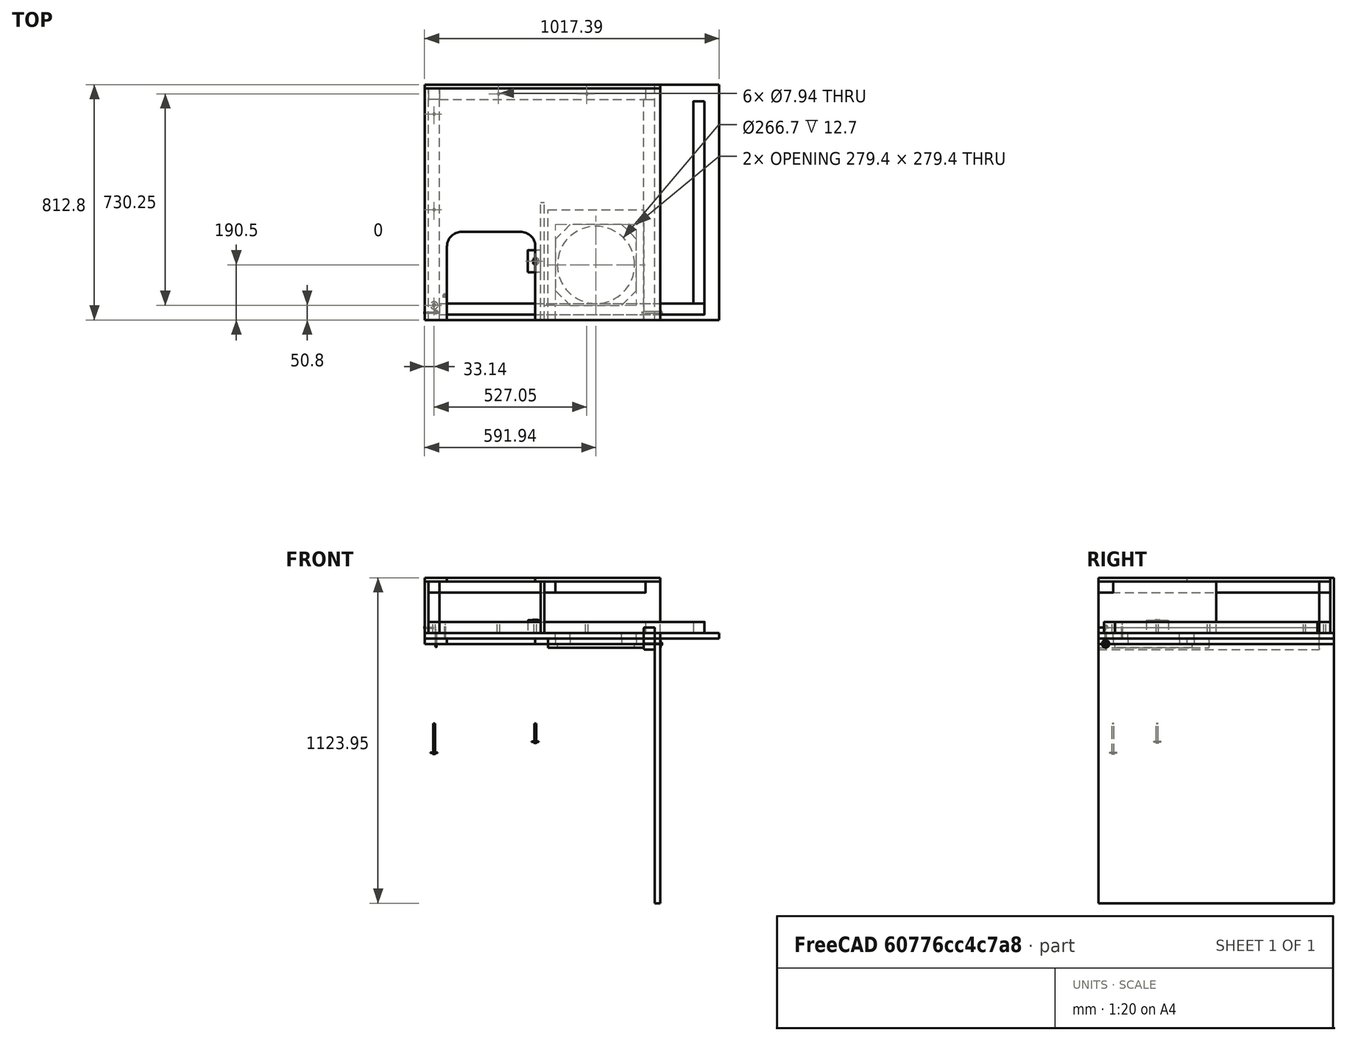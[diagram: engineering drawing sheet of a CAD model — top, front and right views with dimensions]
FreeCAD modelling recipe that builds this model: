
FCSTD DOCUMENT  (FreeCAD 0.20R)
Label: Assembly
License: Creative Commons Attribution
LicenseURL: http://creativecommons.org/licenses/by/4.0/
objects: App::Link×135, Sketcher::SketchObject×20, Part::Extrusion×20, App::LinkGroup×17, Part::Feature×9, Part::Cut×6, App::DocumentObjectGroup×1, Part::Cylinder×1, Mesh::Feature×1
note: 56 computed .brp shape members not serialized (recipe doc carries the construction recipe); baked Part::Feature solids carry a one-line shape summary decoded from their .brp

FEATURE [Sketcher::SketchObject] Sketch004  label="Sketch_H_Inlet_Wall"
  FullyConstrained = false
  sketch-geometry (12):
    g0: LineSegment StartX=0 StartY=0 StartZ=0 EndX=812.8 EndY=0 EndZ=0
    g1: LineSegment StartX=812.8 StartY=0 StartZ=0 EndX=812.8 EndY=812.8 EndZ=0
    g2: LineSegment StartX=812.8 StartY=812.8 StartZ=0 EndX=0 EndY=812.8 EndZ=0
    g3: LineSegment StartX=0 StartY=812.8 StartZ=0 EndX=0 EndY=0 EndZ=0
    g4: LineSegment StartX=730.25 StartY=101.6 StartZ=0 EndX=730.25 EndY=279.4 EndZ=0
    g5: LineSegment StartX=730.25 StartY=279.4 StartZ=0 EndX=679.45 EndY=330.2 EndZ=0
    g6: LineSegment StartX=679.45 StartY=330.2 StartZ=0 EndX=501.65 EndY=330.2 EndZ=0
    g7: LineSegment StartX=501.65 StartY=330.2 StartZ=0 EndX=450.85 EndY=279.4 EndZ=0
    g8: LineSegment StartX=450.85 StartY=279.4 StartZ=0 EndX=450.85 EndY=101.6 EndZ=0
    g9: LineSegment StartX=450.85 StartY=101.6 StartZ=0 EndX=501.65 EndY=50.8 EndZ=0
    g10: LineSegment StartX=501.65 StartY=50.8 StartZ=0 EndX=679.45 EndY=50.8 EndZ=0
    g11: LineSegment StartX=679.45 StartY=50.8 StartZ=0 EndX=730.25 EndY=101.6 EndZ=0
  constraints (35):
    c: Coincident(g0,g1)
    c: Coincident(g1,g2)
    c: Coincident(g2,g3)
    c: Coincident(g3,g0)
    c: Horizontal(g0)
    c: Horizontal(g2)
    c: Vertical(g1)
    c: Vertical(g3)
    c: Coincident(g0,g-1)
    c: DistanceX(g0,g0) = 812.8
    c: DistanceY(g3,g3) = 812.8
    c: Vertical(g4)
    c: Coincident(g4,g5)
    c: Coincident(g5,g6)
    c: Horizontal(g6)
    c: Coincident(g6,g7)
    c: Coincident(g7,g8)
    c: Vertical(g8)
    c: Coincident(g8,g9)
    c: Coincident(g9,g10)
    c: Horizontal(g10)
    c: Coincident(g10,g11)
    c: Coincident(g11,g4)
    c: DistanceX(g4,g0) = 82.55
    c: DistanceY(g0,g10) = 50.8
    c: DistanceX(g8,g9) = 50.8
    c: Perpendicular(g7,g9)
    c: DistanceX(g8,g4) = 279.4
    c: Equal(g8,g6)
    c: Equal(g6,g4)
    c: Equal(g4,g10)
    c: Equal(g9,g7)
    c: Equal(g7,g5)
    c: Equal(g5,g11)
    c: DistanceY(g9,g8) = 50.8
FEATURE [Part::Extrusion] Extrude004  label="Part_H_Inlet_Wall"
  Base = -> Sketch004
  Dir = (0,0,1)
  DirMode = 2
  FaceMakerClass = Part::FaceMakerBullseye
  LengthFwd = 19.05
  LengthRev = 0
  Solid = true
  Symmetric = false
FEATURE [Sketcher::SketchObject] Sketch005  label="Sketch_I_Fan_Mount"
  FullyConstrained = false
  sketch-geometry (5):
    g0: LineSegment StartX=0 StartY=0 StartZ=0 EndX=330.2 EndY=0 EndZ=0
    g1: LineSegment StartX=330.2 StartY=0 StartZ=0 EndX=330.2 EndY=381 EndZ=0
    g2: LineSegment StartX=330.2 StartY=381 StartZ=0 EndX=0 EndY=381 EndZ=0
    g3: LineSegment StartX=0 StartY=381 StartZ=0 EndX=0 EndY=0 EndZ=0
    g4: Circle CenterX=165.1 CenterY=190.5 CenterZ=0 NormalX=0 NormalY=0 NormalZ=1 AngleXU=0 Radius=133.35
  constraints (13):
    c: Coincident(g0,g1)
    c: Coincident(g1,g2)
    c: Coincident(g2,g3)
    c: Coincident(g3,g0)
    c: Horizontal(g0)
    c: Horizontal(g2)
    c: Vertical(g1)
    c: Vertical(g3)
    c: Coincident(g0,g-1)
    c: DistanceY(g3,g3) = 381
    c: DistanceX(g0,g0) = 330.2
    c: Diameter(g4) = 266.7
    c: Symmetric(g0,g1,g4)
FEATURE [Part::Extrusion] Extrude005  label="Part_I_Fan_Mount"
  Base = -> Sketch005
  Dir = (0,0,1)
  DirMode = 2
  FaceMakerClass = Part::FaceMakerBullseye
  LengthFwd = 12.7
  LengthRev = 0
  Placement = pos=(755.65,0,-19.05) rot=(0,1,0;3.14159rad)
  Solid = true
  Symmetric = false
FEATURE [Part::Feature] Part__Feature  label="FAN_W2E250-HJ32-01"
  Placement = pos=(590.55,190.5,-19.05) rot=(1,0,0;1.5708rad)
  shape: bbox 300.2 x 295.3 x 80.4 mm, 902 faces, 0 solids (baked)
FEATURE [Sketcher::SketchObject] Sketch006  label="Sketch_2x2_rail"
  FullyConstrained = false
  sketch-geometry (8):
    g0: LineSegment StartX=0 StartY=34.925 StartZ=0 EndX=0 EndY=3.175 EndZ=0
    g1: ArcOfCircle CenterX=3.175 CenterY=34.925 CenterZ=0 NormalX=0 NormalY=0 NormalZ=1 AngleXU=0 Radius=3.175 StartAngle=1.5708 EndAngle=3.14159
    g2: LineSegment StartX=3.175 StartY=38.1 StartZ=0 EndX=34.925 EndY=38.1 EndZ=0
    g3: ArcOfCircle CenterX=34.925 CenterY=34.925 CenterZ=0 NormalX=0 NormalY=0 NormalZ=1 AngleXU=0 Radius=3.175 StartAngle=4e-16 EndAngle=1.5708
    g4: LineSegment StartX=38.1 StartY=34.925 StartZ=0 EndX=38.1 EndY=3.175 EndZ=0
    g5: ArcOfCircle CenterX=34.925 CenterY=3.175 CenterZ=0 NormalX=0 NormalY=0 NormalZ=1 AngleXU=0 Radius=3.175 StartAngle=4.71239 EndAngle=6.28319
    g6: LineSegment StartX=34.925 StartY=0 StartZ=0 EndX=3.175 EndY=0 EndZ=0
    g7: ArcOfCircle CenterX=3.175 CenterY=3.175 CenterZ=0 NormalX=0 NormalY=0 NormalZ=1 AngleXU=0 Radius=3.175 StartAngle=3.14159 EndAngle=4.71239
  constraints (22):
    c: Vertical(g0)
    c: Tangent(g0,g1) = -1.5708
    c: Radius(g1) = 3.175
    c: Angle(g1) = 1.5708
    c: Coincident(g2,g1)
    c: Horizontal(g2)
    c: Tangent(g2,g3) = 1.5708
    c: Coincident(g4,g3)
    c: Vertical(g4)
    c: Tangent(g5,g4) = 1.5708
    c: Horizontal(g6)
    c: Tangent(g6,g5) = 1.5708
    c: Tangent(g7,g6) = 1.5708
    c: Tangent(g7,g0) = -1.5708
    c: Equal(g1,g7)
    c: Equal(g7,g3)
    c: Equal(g2,g0)
    c: Equal(g0,g6)
    c: Equal(g6,g4)
    c: PointOnObject(g-1,g0)
    c: PointOnObject(g6,g-1)
    c: DistanceX(g0,g4) = 38.1
FEATURE [Part::Extrusion] Extrude006  label="IF_A"
  Base = -> Sketch006
  Dir = (0,0,1)
  DirMode = 2
  FaceMakerClass = Part::FaceMakerBullseye
  LengthFwd = 762
  LengthRev = 0
  Placement = pos=(793.75,0,1e-14) rot=(0.57735,-0.57735,-0.57735;4.18879rad)
  Solid = true
  Symmetric = false
FEATURE [Sketcher::SketchObject] Sketch007  label="Sketch_H_Inlet_Wall001"
  FullyConstrained = false
  sketch-geometry (12):
    g0: LineSegment StartX=0 StartY=0 StartZ=0 EndX=330.2 EndY=0 EndZ=0
    g1: LineSegment StartX=330.2 StartY=0 StartZ=0 EndX=330.2 EndY=381 EndZ=0
    g2: LineSegment StartX=330.2 StartY=381 StartZ=0 EndX=0 EndY=381 EndZ=0
    g3: LineSegment StartX=0 StartY=381 StartZ=0 EndX=0 EndY=0 EndZ=0
    g4: LineSegment StartX=304.8 StartY=101.6 StartZ=0 EndX=304.8 EndY=279.4 EndZ=0
    g5: LineSegment StartX=304.8 StartY=279.4 StartZ=0 EndX=254 EndY=330.2 EndZ=0
    g6: LineSegment StartX=254 StartY=330.2 StartZ=0 EndX=76.2 EndY=330.2 EndZ=0
    g7: LineSegment StartX=76.2 StartY=330.2 StartZ=0 EndX=25.4 EndY=279.4 EndZ=0
    g8: LineSegment StartX=25.4 StartY=279.4 StartZ=0 EndX=25.4 EndY=101.6 EndZ=0
    g9: LineSegment StartX=25.4 StartY=101.6 StartZ=0 EndX=76.2 EndY=50.8 EndZ=0
    g10: LineSegment StartX=76.2 StartY=50.8 StartZ=0 EndX=254 EndY=50.8 EndZ=0
    g11: LineSegment StartX=254 StartY=50.8 StartZ=0 EndX=304.8 EndY=101.6 EndZ=0
  constraints (35):
    c: Coincident(g0,g1)
    c: Coincident(g1,g2)
    c: Coincident(g2,g3)
    c: Coincident(g3,g0)
    c: Horizontal(g0)
    c: Horizontal(g2)
    c: Vertical(g1)
    c: Vertical(g3)
    c: Coincident(g0,g-1)
    c: DistanceX(g0,g0) = 330.2
    c: DistanceY(g3,g3) = 381
    c: Vertical(g4)
    c: Coincident(g4,g5)
    c: Coincident(g5,g6)
    c: Horizontal(g6)
    c: Coincident(g6,g7)
    c: Coincident(g7,g8)
    c: Vertical(g8)
    c: Coincident(g8,g9)
    c: Coincident(g9,g10)
    c: Horizontal(g10)
    c: Coincident(g10,g11)
    c: Coincident(g11,g4)
    c: DistanceX(g7,g4) = 279.4
    c: DistanceX(g4,g0) = 25.4
    c: DistanceY(g0,g10) = 50.8
    c: DistanceX(g8,g9) = 50.8
    c: Perpendicular(g11,g9)
    c: Equal(g6,g10)
    c: Equal(g10,g8)
    c: Equal(g8,g4)
    c: Equal(g7,g11)
    c: Equal(g11,g9)
    c: Equal(g9,g5)
    c: DistanceY(g9,g8) = 50.8
FEATURE [Part::Extrusion] Extrude007  label="Fan_Spacer"
  Base = -> Sketch007
  Dir = (0,0,1)
  DirMode = 2
  FaceMakerClass = Part::FaceMakerBullseye
  LengthFwd = 19.05
  LengthRev = 0
  Placement = pos=(755.65,0,4.3e-14) rot=(0,1,0;3.14159rad)
  Solid = true
  Symmetric = false
FEATURE [Part::Feature] Screw_w_Washer_B
  Placement = pos=(38.1,25.4,19.05) rot=(0,1,0;3.14159rad)
  shape: bbox 15.88 x 15.88 x 50.8 mm, 35 faces (baked)
FEATURE [App::Link] Link001  label="Screw_w_Washer_B001"
  LinkPlacement = pos=(38.1,736.601,19.05) rot=(0,1,0;3.14159rad)
  LinkedObject = -> Screw_w_Washer_B
  Placement = pos=(38.1,736.601,19.05) rot=(0,1,0;3.14159rad)
FEATURE [App::Link] Link002  label="Screw_w_Washer_B002"
  LinkPlacement = pos=(38.1,152.4,19.05) rot=(1,0,0;3.14159rad)
  LinkedObject = -> Screw_w_Washer_B
  Placement = pos=(38.1,152.4,19.05) rot=(1,0,0;3.14159rad)
FEATURE [App::Link] Link003  label="Screw_w_Washer_B003"
  LinkPlacement = pos=(38.1,609.6,19.0501) rot=(1,0,0;3.14159rad)
  LinkedObject = -> Screw_w_Washer_B
  Placement = pos=(38.1,609.6,19.0501) rot=(1,0,0;3.14159rad)
FEATURE [App::Link] Link004  label="Screw_w_Washer_B004"
  LinkPlacement = pos=(38.1,304.8,19.05) rot=(0,1,0;3.14159rad)
  LinkedObject = -> Screw_w_Washer_B
  Placement = pos=(38.1,304.8,19.05) rot=(0,1,0;3.14159rad)
FEATURE [App::Link] Link005  label="Screw_w_Washer_B005"
  LinkPlacement = pos=(38.1,457.2,19.05) rot=(0,1,0;3.14159rad)
  LinkedObject = -> Screw_w_Washer_B
  Placement = pos=(38.1,457.2,19.05) rot=(0,1,0;3.14159rad)
FEATURE [App::Link] Link006  label="Screw_w_Washer_B006"
  LinkTransform = true
  LinkedObject = -> Screw_w_Washer_B
FEATURE [App::Link] Link007  label="Screw_w_Washer_B007"
  LinkTransform = true
  LinkedObject = -> Link001
FEATURE [App::Link] Link008  label="Screw_w_Washer_B008"
  LinkTransform = true
  LinkedObject = -> Link002
FEATURE [App::Link] Link009  label="Screw_w_Washer_B009"
  LinkTransform = true
  LinkedObject = -> Link003
FEATURE [App::Link] Link010  label="Screw_w_Washer_B010"
  LinkTransform = true
  LinkedObject = -> Link004
FEATURE [App::Link] Link011  label="Screw_w_Washer_B011"
  LinkTransform = true
  LinkedObject = -> Link005
FEATURE [App::LinkGroup] LinkGroup
  ElementList = -> [Link006,Link007,Link008,Link009,Link010,Link011]
  LinkMode = 1
  Placement = pos=(736.6,-6.10352e-05,0) rot=(0,0,1;0rad)
FEATURE [App::Link] Link012  label="Screw_w_Washer_B012"
  LinkPlacement = pos=(450.85,50.8,-31.75) rot=(0,0,1;0rad)
  LinkedObject = -> Screw_w_Washer_B
  Placement = pos=(450.85,50.8,-31.75) rot=(0,0,1;0rad)
FEATURE [App::Link] Link013  label="Screw_w_Washer_B013"
  LinkPlacement = pos=(590.55,355.6,-31.75) rot=(0,0,1;1.5708rad)
  LinkedObject = -> Screw_w_Washer_B
  Placement = pos=(590.55,355.6,-31.75) rot=(0,0,1;1.5708rad)
FEATURE [App::Link] Link014  label="Screw_w_Washer_B014"
  LinkPlacement = pos=(438.15,190.5,-31.75) rot=(0,0,1;3.14159rad)
  LinkedObject = -> Screw_w_Washer_B
  Placement = pos=(438.15,190.5,-31.75) rot=(0,0,1;3.14159rad)
FEATURE [App::Link] Link015  label="Screw_w_Washer_B015"
  LinkPlacement = pos=(450.85,330.2,-31.75) rot=(0,0,-1;1.5708rad)
  LinkedObject = -> Screw_w_Washer_B
  Placement = pos=(450.85,330.2,-31.75) rot=(0,0,-1;1.5708rad)
FEATURE [App::Link] Link016  label="Screw_w_Washer_B016"
  LinkPlacement = pos=(590.55,25.3999,-31.75) rot=(0,0,1;0rad)
  LinkedObject = -> Screw_w_Washer_B
  Placement = pos=(590.55,25.3999,-31.75) rot=(0,0,1;0rad)
FEATURE [App::Link] Link017  label="Screw_w_Washer_B017"
  LinkPlacement = pos=(730.25,50.7999,-31.75) rot=(0,0,1;1.5708rad)
  LinkedObject = -> Screw_w_Washer_B
  Placement = pos=(730.25,50.7999,-31.75) rot=(0,0,1;1.5708rad)
FEATURE [App::Link] Link018  label="Screw_w_Washer_B018"
  LinkPlacement = pos=(742.95,190.5,-31.75) rot=(0,0,1;3.14159rad)
  LinkedObject = -> Screw_w_Washer_B
  Placement = pos=(742.95,190.5,-31.75) rot=(0,0,1;3.14159rad)
FEATURE [App::Link] Link019  label="Screw_w_Washer_B019"
  LinkPlacement = pos=(730.25,330.2,-31.75) rot=(0,0,1;3.14159rad)
  LinkedObject = -> Screw_w_Washer_B
  Placement = pos=(730.25,330.2,-31.75) rot=(0,0,1;3.14159rad)
FEATURE [App::DocumentObjectGroup] Group
  Group = -> [Link012,Link013,Link014,Link015,Link016,Link017,Link018,Link019,Part__Feature,Extrude005,Extrude007]
FEATURE [App::LinkGroup] LinkGroup001
  ElementList = -> [Group]
  LinkMode = 0
  Placement = pos=(3.05176e-05,-0.000106812,6.67572e-05) rot=(0,0,1;0rad)
FEATURE [Sketcher::SketchObject] Sketch  label="Sketch_2x2_rail001"
  FullyConstrained = false
  sketch-geometry (8):
    g0: LineSegment StartX=0 StartY=34.925 StartZ=0 EndX=0 EndY=3.175 EndZ=0
    g1: ArcOfCircle CenterX=3.175 CenterY=34.925 CenterZ=0 NormalX=0 NormalY=0 NormalZ=1 AngleXU=0 Radius=3.175 StartAngle=1.5708 EndAngle=3.14159
    g2: LineSegment StartX=3.175 StartY=38.1 StartZ=0 EndX=34.925 EndY=38.1 EndZ=0
    g3: ArcOfCircle CenterX=34.925 CenterY=34.925 CenterZ=0 NormalX=0 NormalY=0 NormalZ=1 AngleXU=0 Radius=3.175 StartAngle=2.2e-15 EndAngle=1.5708
    g4: LineSegment StartX=38.1 StartY=34.925 StartZ=0 EndX=38.1 EndY=3.175 EndZ=0
    g5: ArcOfCircle CenterX=34.925 CenterY=3.175 CenterZ=0 NormalX=0 NormalY=0 NormalZ=1 AngleXU=0 Radius=3.175 StartAngle=4.71239 EndAngle=6.28319
    g6: LineSegment StartX=34.925 StartY=0 StartZ=0 EndX=3.175 EndY=0 EndZ=0
    g7: ArcOfCircle CenterX=3.175 CenterY=3.175 CenterZ=0 NormalX=0 NormalY=0 NormalZ=1 AngleXU=0 Radius=3.175 StartAngle=3.14159 EndAngle=4.71239
  constraints (22):
    c: Vertical(g0)
    c: Tangent(g0,g1) = -1.5708
    c: Radius(g1) = 3.175
    c: Angle(g1) = 1.5708
    c: Coincident(g2,g1)
    c: Horizontal(g2)
    c: Tangent(g2,g3) = 1.5708
    c: Coincident(g4,g3)
    c: Vertical(g4)
    c: Tangent(g5,g4) = 1.5708
    c: Horizontal(g6)
    c: Tangent(g6,g5) = 1.5708
    c: Tangent(g7,g6) = 1.5708
    c: Tangent(g7,g0) = -1.5708
    c: Equal(g1,g7)
    c: Equal(g7,g3)
    c: Equal(g2,g0)
    c: Equal(g0,g6)
    c: Equal(g6,g4)
    c: PointOnObject(g-1,g0)
    c: PointOnObject(g6,g-1)
    c: DistanceX(g0,g4) = 38.1
FEATURE [Part::Extrusion] Extrude  label="BF_A"
  Base = -> Sketch
  Dir = (0,0,1)
  DirMode = 2
  FaceMakerClass = Part::FaceMakerBullseye
  LengthFwd = 800.1
  LengthRev = 0
  Placement = pos=(12.7,4.4e-14,196.85) rot=(-1,0,0;1.5708rad)
  Solid = true
  Symmetric = false
FEATURE [Sketcher::SketchObject] Sketch008  label="Sketch_D_Baffle_Ext_Wall"
  FullyConstrained = false
  sketch-geometry (10):
    g0: LineSegment StartX=0 StartY=0 StartZ=0 EndX=0 EndY=800.1 EndZ=0
    g1: LineSegment StartX=0 StartY=800.1 StartZ=0 EndX=812.8 EndY=800.1 EndZ=0
    g2: LineSegment StartX=812.8 StartY=800.1 StartZ=0 EndX=812.8 EndY=0 EndZ=0
    g3: LineSegment StartX=812.8 StartY=0 StartZ=0 EndX=736.6 EndY=0 EndZ=0
    g4: LineSegment StartX=736.6 StartY=0 StartZ=0 EndX=736.6 EndY=254 EndZ=0
    g5: LineSegment StartX=685.8 StartY=304.8 StartZ=0 EndX=482.6 EndY=304.8 EndZ=0
    g6: LineSegment StartX=431.8 StartY=254 StartZ=0 EndX=431.8 EndY=0 EndZ=0
    g7: LineSegment StartX=431.8 StartY=0 StartZ=0 EndX=0 EndY=0 EndZ=0
    g8: ArcOfCircle CenterX=482.6 CenterY=254 CenterZ=0 NormalX=0 NormalY=0 NormalZ=1 AngleXU=0 Radius=50.8 StartAngle=1.5708 EndAngle=3.14159
    g9: ArcOfCircle CenterX=685.8 CenterY=254 CenterZ=0 NormalX=0 NormalY=0 NormalZ=1 AngleXU=0 Radius=50.8 StartAngle=0 EndAngle=1.5708
  constraints (27):
    c: Coincident(g-1,g0)
    c: PointOnObject(g0,g-2)
    c: Coincident(g0,g1)
    c: Horizontal(g1)
    c: Coincident(g1,g2)
    c: PointOnObject(g2,g-1)
    c: Vertical(g2)
    c: Coincident(g2,g3)
    c: PointOnObject(g3,g-1)
    c: Coincident(g3,g4)
    c: Vertical(g4)
    c: Horizontal(g5)
    c: PointOnObject(g6,g-1)
    c: Vertical(g6)
    c: Coincident(g6,g7)
    c: Coincident(g7,g0)
    c: DistanceY(g0,g0) = 800.1
    c: DistanceX(g1,g1) = 812.8
    c: DistanceX(g3,g3) = 76.2
    c: DistanceX(g6,g3) = 304.8
    c: DistanceY(g6,g5) = 304.8
    c: Equal(g8,g9)
    c: Tangent(g8,g6) = -1.5708
    c: Tangent(g9,g4) = -1.5708
    c: Tangent(g9,g5) = -1.5708
    c: Tangent(g8,g5) = -1.5708
    c: Radius(g8) = 50.8
FEATURE [Part::Extrusion] Extrude008  label="Part_D_Baffle_Ext_Wall_001"
  Base = -> Sketch008
  Dir = (0,0,1)
  DirMode = 2
  FaceMakerClass = Part::FaceMakerBullseye
  LengthFwd = 12.7
  LengthRev = 0
  Placement = pos=(812.8,0,209.55) rot=(0,1,0;3.14159rad)
  Solid = true
  Symmetric = false
FEATURE [Sketcher::SketchObject] Sketch009  label="Sketch_G_Baffle_Half_Wall"
  FullyConstrained = false
  sketch-geometry (4):
    g0: LineSegment StartX=0 StartY=0 StartZ=0 EndX=406.4 EndY=0 EndZ=0
    g1: LineSegment StartX=406.4 StartY=0 StartZ=0 EndX=406.4 EndY=177.8 EndZ=0
    g2: LineSegment StartX=406.4 StartY=177.8 StartZ=0 EndX=0 EndY=177.8 EndZ=0
    g3: LineSegment StartX=0 StartY=177.8 StartZ=0 EndX=0 EndY=0 EndZ=0
  constraints (11):
    c: Coincident(g0,g1)
    c: Coincident(g1,g2)
    c: Coincident(g2,g3)
    c: Coincident(g3,g0)
    c: Horizontal(g0)
    c: Horizontal(g2)
    c: Vertical(g1)
    c: Vertical(g3)
    c: Coincident(g0,g-1)
    c: DistanceY(g3,g3) = 177.8
    c: DistanceX(g0,g0) = 406.4
FEATURE [Part::Extrusion] Extrude009  label="Part_G_Baffle_Half_Wall_001"
  Base = -> Sketch009
  Dir = (0,0,1)
  DirMode = 2
  FaceMakerClass = Part::FaceMakerBullseye
  LengthFwd = 12.7
  LengthRev = 0
  Placement = pos=(400.05,-8.5e-14,19.05) rot=(0.57735,0.57735,0.57735;2.0944rad)
  Solid = true
  Symmetric = false
FEATURE [Sketcher::SketchObject] Sketch010  label="Sketch_E_Baffle_Top"
  FullyConstrained = false
  sketch-geometry (4):
    g0: LineSegment StartX=0 StartY=0 StartZ=0 EndX=812.8 EndY=0 EndZ=0
    g1: LineSegment StartX=812.8 StartY=0 StartZ=0 EndX=812.8 EndY=190.5 EndZ=0
    g2: LineSegment StartX=812.8 StartY=190.5 StartZ=0 EndX=0 EndY=190.5 EndZ=0
    g3: LineSegment StartX=0 StartY=190.5 StartZ=0 EndX=0 EndY=0 EndZ=0
  constraints (11):
    c: Coincident(g0,g1)
    c: Coincident(g1,g2)
    c: Coincident(g2,g3)
    c: Coincident(g3,g0)
    c: Horizontal(g0)
    c: Horizontal(g2)
    c: Vertical(g1)
    c: Vertical(g3)
    c: Coincident(g0,g-1)
    c: DistanceY(g3,g3) = 190.5
    c: DistanceX(g0,g0) = 812.8
FEATURE [Part::Extrusion] Extrude010  label="Part_E_Baffle_Top_001"
  Base = -> Sketch010
  Dir = (0,0,1)
  DirMode = 2
  FaceMakerClass = Part::FaceMakerBullseye
  LengthFwd = 12.7
  LengthRev = 0
  Placement = pos=(0,812.8,19.05) rot=(1,0,0;1.5708rad)
  Solid = true
  Symmetric = false
FEATURE [Sketcher::SketchObject] Sketch012  label="Sketch_F_Baffle_Side_Wall"
  FullyConstrained = false
  sketch-geometry (4):
    g0: LineSegment StartX=0 StartY=0 StartZ=0 EndX=800.1 EndY=0 EndZ=0
    g1: LineSegment StartX=800.1 StartY=0 StartZ=0 EndX=800.1 EndY=177.8 EndZ=0
    g2: LineSegment StartX=800.1 StartY=177.8 StartZ=0 EndX=0 EndY=177.8 EndZ=0
    g3: LineSegment StartX=0 StartY=177.8 StartZ=0 EndX=0 EndY=0 EndZ=0
  constraints (11):
    c: Coincident(g0,g1)
    c: Coincident(g1,g2)
    c: Coincident(g2,g3)
    c: Coincident(g3,g0)
    c: Horizontal(g0)
    c: Horizontal(g2)
    c: Vertical(g1)
    c: Vertical(g3)
    c: Coincident(g0,g-1)
    c: DistanceY(g3,g3) = 177.8
    c: DistanceX(g0,g0) = 800.1
FEATURE [Part::Extrusion] Extrude012  label="Part_F_Baffle_Side_Wall_001"
  Base = -> Sketch012
  Dir = (0,0,1)
  DirMode = 2
  FaceMakerClass = Part::FaceMakerBullseye
  LengthFwd = 12.7
  LengthRev = 0
  Placement = pos=(-4e-15,-8e-15,19.05) rot=(0.57735,0.57735,0.57735;2.0944rad)
  Solid = true
  Symmetric = false
FEATURE [Sketcher::SketchObject] Sketch013  label="Sketch_2x2_rail002"
  FullyConstrained = false
  sketch-geometry (8):
    g0: LineSegment StartX=0 StartY=34.925 StartZ=0 EndX=0 EndY=3.175 EndZ=0
    g1: ArcOfCircle CenterX=3.175 CenterY=34.925 CenterZ=0 NormalX=0 NormalY=0 NormalZ=1 AngleXU=0 Radius=3.175 StartAngle=1.5708 EndAngle=3.14159
    g2: LineSegment StartX=3.175 StartY=38.1 StartZ=0 EndX=34.925 EndY=38.1 EndZ=0
    g3: ArcOfCircle CenterX=34.925 CenterY=34.925 CenterZ=0 NormalX=0 NormalY=0 NormalZ=1 AngleXU=0 Radius=3.175 StartAngle=1.1e-15 EndAngle=1.5708
    g4: LineSegment StartX=38.1 StartY=34.925 StartZ=0 EndX=38.1 EndY=3.175 EndZ=0
    g5: ArcOfCircle CenterX=34.925 CenterY=3.175 CenterZ=0 NormalX=0 NormalY=0 NormalZ=1 AngleXU=0 Radius=3.175 StartAngle=4.71239 EndAngle=6.28319
    g6: LineSegment StartX=34.925 StartY=4e-16 StartZ=0 EndX=3.175 EndY=4e-16 EndZ=0
    g7: ArcOfCircle CenterX=3.175 CenterY=3.175 CenterZ=0 NormalX=0 NormalY=0 NormalZ=1 AngleXU=0 Radius=3.175 StartAngle=3.14159 EndAngle=4.71239
  constraints (22):
    c: Vertical(g0)
    c: Tangent(g0,g1) = -1.5708
    c: Radius(g1) = 3.175
    c: Angle(g1) = 1.5708
    c: Coincident(g2,g1)
    c: Horizontal(g2)
    c: Tangent(g2,g3) = 1.5708
    c: Coincident(g4,g3)
    c: Vertical(g4)
    c: Tangent(g5,g4) = 1.5708
    c: Horizontal(g6)
    c: Tangent(g6,g5) = 1.5708
    c: Tangent(g7,g6) = 1.5708
    c: Tangent(g7,g0) = -1.5708
    c: Equal(g1,g7)
    c: Equal(g7,g3)
    c: Equal(g2,g0)
    c: Equal(g0,g6)
    c: Equal(g6,g4)
    c: PointOnObject(g-1,g0)
    c: PointOnObject(g6,g-1)
    c: DistanceX(g0,g4) = 38.1
FEATURE [Part::Extrusion] Extrude013  label="BF_C"
  Base = -> Sketch013
  Dir = (0,0,1)
  DirMode = 2
  FaceMakerClass = Part::FaceMakerBullseye
  LengthFwd = 139.7
  LengthRev = 0
  Placement = pos=(12.7,762,19.05) rot=(0,0,1;0rad)
  Solid = true
  Symmetric = false
FEATURE [Sketcher::SketchObject] Sketch014  label="Sketch_2x2_rail003"
  FullyConstrained = false
  sketch-geometry (8):
    g0: LineSegment StartX=0 StartY=34.925 StartZ=0 EndX=0 EndY=3.175 EndZ=0
    g1: ArcOfCircle CenterX=3.175 CenterY=34.925 CenterZ=0 NormalX=0 NormalY=0 NormalZ=1 AngleXU=0 Radius=3.175 StartAngle=1.5708 EndAngle=3.14159
    g2: LineSegment StartX=3.175 StartY=38.1 StartZ=0 EndX=34.925 EndY=38.1 EndZ=0
    g3: ArcOfCircle CenterX=34.925 CenterY=34.925 CenterZ=0 NormalX=0 NormalY=0 NormalZ=1 AngleXU=0 Radius=3.175 StartAngle=9e-16 EndAngle=1.5708
    g4: LineSegment StartX=38.1 StartY=34.925 StartZ=0 EndX=38.1 EndY=3.175 EndZ=0
    g5: ArcOfCircle CenterX=34.925 CenterY=3.175 CenterZ=0 NormalX=0 NormalY=0 NormalZ=1 AngleXU=0 Radius=3.175 StartAngle=4.71239 EndAngle=6.28319
    g6: LineSegment StartX=34.925 StartY=4e-16 StartZ=0 EndX=3.175 EndY=4e-16 EndZ=0
    g7: ArcOfCircle CenterX=3.175 CenterY=3.175 CenterZ=0 NormalX=0 NormalY=0 NormalZ=1 AngleXU=0 Radius=3.175 StartAngle=3.14159 EndAngle=4.71239
  constraints (22):
    c: Vertical(g0)
    c: Tangent(g0,g1) = -1.5708
    c: Radius(g1) = 3.175
    c: Angle(g1) = 1.5708
    c: Coincident(g2,g1)
    c: Horizontal(g2)
    c: Tangent(g2,g3) = 1.5708
    c: Coincident(g4,g3)
    c: Vertical(g4)
    c: Tangent(g5,g4) = 1.5708
    c: Horizontal(g6)
    c: Tangent(g6,g5) = 1.5708
    c: Tangent(g7,g6) = 1.5708
    c: Tangent(g7,g0) = -1.5708
    c: Equal(g1,g7)
    c: Equal(g7,g3)
    c: Equal(g2,g0)
    c: Equal(g0,g6)
    c: Equal(g6,g4)
    c: PointOnObject(g-1,g0)
    c: PointOnObject(g6,g-1)
    c: DistanceX(g0,g4) = 38.1
FEATURE [Part::Extrusion] Extrude014  label="BF_B"
  Base = -> Sketch014
  Dir = (0,0,1)
  DirMode = 2
  FaceMakerClass = Part::FaceMakerBullseye
  LengthFwd = 711.2
  LengthRev = 0
  Placement = pos=(50.8,800.1,196.85) rot=(0.57735,-0.57735,0.57735;4.18879rad)
  Solid = true
  Symmetric = false
FEATURE [Sketcher::SketchObject] Sketch015  label="Sketch_2x2_rail004"
  FullyConstrained = false
  sketch-geometry (8):
    g0: LineSegment StartX=0 StartY=34.925 StartZ=0 EndX=0 EndY=3.175 EndZ=0
    g1: ArcOfCircle CenterX=3.175 CenterY=34.925 CenterZ=0 NormalX=0 NormalY=0 NormalZ=1 AngleXU=0 Radius=3.175 StartAngle=1.5708 EndAngle=3.14159
    g2: LineSegment StartX=3.175 StartY=38.1 StartZ=0 EndX=34.925 EndY=38.1 EndZ=0
    g3: ArcOfCircle CenterX=34.925 CenterY=34.925 CenterZ=0 NormalX=0 NormalY=0 NormalZ=1 AngleXU=0 Radius=3.175 StartAngle=1.2e-15 EndAngle=1.5708
    g4: LineSegment StartX=38.1 StartY=34.925 StartZ=0 EndX=38.1 EndY=3.175 EndZ=0
    g5: ArcOfCircle CenterX=34.925 CenterY=3.175 CenterZ=0 NormalX=0 NormalY=0 NormalZ=1 AngleXU=0 Radius=3.175 StartAngle=4.71239 EndAngle=6.28319
    g6: LineSegment StartX=34.925 StartY=0 StartZ=0 EndX=3.175 EndY=0 EndZ=0
    g7: ArcOfCircle CenterX=3.175 CenterY=3.175 CenterZ=0 NormalX=0 NormalY=0 NormalZ=1 AngleXU=0 Radius=3.175 StartAngle=3.14159 EndAngle=4.71239
  constraints (22):
    c: Vertical(g0)
    c: Tangent(g0,g1) = -1.5708
    c: Radius(g1) = 3.175
    c: Angle(g1) = 1.5708
    c: Coincident(g2,g1)
    c: Horizontal(g2)
    c: Tangent(g2,g3) = 1.5708
    c: Coincident(g4,g3)
    c: Vertical(g4)
    c: Tangent(g5,g4) = 1.5708
    c: Horizontal(g6)
    c: Tangent(g6,g5) = 1.5708
    c: Tangent(g7,g6) = 1.5708
    c: Tangent(g7,g0) = -1.5708
    c: Equal(g1,g7)
    c: Equal(g7,g3)
    c: Equal(g2,g0)
    c: Equal(g0,g6)
    c: Equal(g6,g4)
    c: PointOnObject(g-1,g0)
    c: PointOnObject(g6,g-1)
    c: DistanceX(g0,g4) = 38.1
FEATURE [Part::Extrusion] Extrude015  label="BF_D"
  Base = -> Sketch015
  Dir = (0,0,1)
  DirMode = 2
  FaceMakerClass = Part::FaceMakerBullseye
  LengthFwd = 762
  LengthRev = 0
  Placement = pos=(12.7,2.4e-14,19.05) rot=(0.57735,0.57735,0.57735;4.18879rad)
  Solid = true
  Symmetric = false
FEATURE [Sketcher::SketchObject] Sketch016  label="Sketch_2x2_rail005"
  FullyConstrained = false
  sketch-geometry (8):
    g0: LineSegment StartX=0 StartY=34.925 StartZ=0 EndX=0 EndY=3.175 EndZ=0
    g1: ArcOfCircle CenterX=3.175 CenterY=34.925 CenterZ=0 NormalX=0 NormalY=0 NormalZ=1 AngleXU=0 Radius=3.175 StartAngle=1.5708 EndAngle=3.14159
    g2: LineSegment StartX=3.175 StartY=38.1 StartZ=0 EndX=34.925 EndY=38.1 EndZ=0
    g3: ArcOfCircle CenterX=34.925 CenterY=34.925 CenterZ=0 NormalX=0 NormalY=0 NormalZ=1 AngleXU=0 Radius=3.175 StartAngle=2.5e-15 EndAngle=1.5708
    g4: LineSegment StartX=38.1 StartY=34.925 StartZ=0 EndX=38.1 EndY=3.175 EndZ=0
    g5: ArcOfCircle CenterX=34.925 CenterY=3.175 CenterZ=0 NormalX=0 NormalY=0 NormalZ=1 AngleXU=0 Radius=3.175 StartAngle=4.71239 EndAngle=6.28319
    g6: LineSegment StartX=34.925 StartY=4e-16 StartZ=0 EndX=3.175 EndY=4e-16 EndZ=0
    g7: ArcOfCircle CenterX=3.175 CenterY=3.175 CenterZ=0 NormalX=0 NormalY=0 NormalZ=1 AngleXU=0 Radius=3.175 StartAngle=3.14159 EndAngle=4.71239
  constraints (22):
    c: Vertical(g0)
    c: Tangent(g0,g1) = -1.5708
    c: Radius(g1) = 3.175
    c: Angle(g1) = 1.5708
    c: Coincident(g2,g1)
    c: Horizontal(g2)
    c: Tangent(g2,g3) = 1.5708
    c: Coincident(g4,g3)
    c: Vertical(g4)
    c: Tangent(g5,g4) = 1.5708
    c: Horizontal(g6)
    c: Tangent(g6,g5) = 1.5708
    c: Tangent(g7,g6) = 1.5708
    c: Tangent(g7,g0) = -1.5708
    c: Equal(g1,g7)
    c: Equal(g7,g3)
    c: Equal(g2,g0)
    c: Equal(g0,g6)
    c: Equal(g6,g4)
    c: PointOnObject(g-1,g0)
    c: PointOnObject(g6,g-1)
    c: DistanceX(g0,g4) = 38.1
FEATURE [Part::Extrusion] Extrude016  label="BF_E"
  Base = -> Sketch016
  Dir = (0,0,1)
  DirMode = 2
  FaceMakerClass = Part::FaceMakerBullseye
  LengthFwd = 50.8
  LengthRev = 0
  Placement = pos=(412.75,8.8e-14,196.85) rot=(-1,0,0;1.5708rad)
  Solid = true
  Symmetric = false
FEATURE [Sketcher::SketchObject] Sketch017  label="Sketch_2x2_rail006"
  FullyConstrained = false
  sketch-geometry (8):
    g0: LineSegment StartX=0 StartY=41.275 StartZ=0 EndX=0 EndY=3.175 EndZ=0
    g1: ArcOfCircle CenterX=3.175 CenterY=41.275 CenterZ=0 NormalX=0 NormalY=0 NormalZ=1 AngleXU=0 Radius=3.175 StartAngle=1.5708 EndAngle=3.14159
    g2: LineSegment StartX=3.175 StartY=44.45 StartZ=0 EndX=41.275 EndY=44.45 EndZ=0
    g3: ArcOfCircle CenterX=41.275 CenterY=41.275 CenterZ=0 NormalX=0 NormalY=0 NormalZ=1 AngleXU=0 Radius=3.175 StartAngle=-9e-16 EndAngle=1.5708
    g4: LineSegment StartX=44.45 StartY=41.275 StartZ=0 EndX=44.45 EndY=3.175 EndZ=0
    g5: ArcOfCircle CenterX=41.275 CenterY=3.175 CenterZ=0 NormalX=0 NormalY=0 NormalZ=1 AngleXU=0 Radius=3.175 StartAngle=4.71239 EndAngle=6.28319
    g6: LineSegment StartX=41.275 StartY=1.3e-15 StartZ=0 EndX=3.175 EndY=1.3e-15 EndZ=0
    g7: ArcOfCircle CenterX=3.175 CenterY=3.175 CenterZ=0 NormalX=0 NormalY=0 NormalZ=1 AngleXU=0 Radius=3.175 StartAngle=3.14159 EndAngle=4.71239
  constraints (22):
    c: Vertical(g0)
    c: Tangent(g0,g1) = -1.5708
    c: Radius(g1) = 3.175
    c: Angle(g1) = 1.5708
    c: Coincident(g2,g1)
    c: Horizontal(g2)
    c: Tangent(g2,g3) = 1.5708
    c: Coincident(g4,g3)
    c: Vertical(g4)
    c: Tangent(g5,g4) = 1.5708
    c: Horizontal(g6)
    c: Tangent(g6,g5) = 1.5708
    c: Tangent(g7,g6) = 1.5708
    c: Tangent(g7,g0) = -1.5708
    c: Equal(g1,g7)
    c: Equal(g7,g3)
    c: Equal(g2,g0)
    c: Equal(g0,g6)
    c: Equal(g6,g4)
    c: PointOnObject(g-1,g0)
    c: PointOnObject(g6,g-1)
    c: DistanceX(g0,g4) = 44.45
FEATURE [Part::Extrusion] Extrude017  label="BF_F"
  Base = -> Sketch017
  Dir = (0,0,1)
  DirMode = 2
  FaceMakerClass = Part::FaceMakerBullseye
  LengthFwd = 76.2
  LengthRev = 0
  Placement = pos=(400.05,165.1,19.05) rot=(0,0.707107,0.707107;3.14159rad)
  Solid = true
  Symmetric = false
FEATURE [App::Link] Link020  label="Part_F_Baffle_Side_Wall_002"
  LinkPlacement = pos=(800.1,9.59848e-05,19.0499) rot=(0.57735,0.57735,0.57735;2.0944rad)
  LinkedObject = -> Extrude012
  Placement = pos=(800.1,9.59848e-05,19.0499) rot=(0.57735,0.57735,0.57735;2.0944rad)
FEATURE [App::Link] Link021  label="BF_A001"
  LinkPlacement = pos=(762,2.34664e-05,196.85) rot=(-1,0,0;1.5708rad)
  LinkedObject = -> Extrude
  Placement = pos=(762,2.34664e-05,196.85) rot=(-1,0,0;1.5708rad)
FEATURE [App::Link] Link022  label="BF_B001"
  LinkPlacement = pos=(50.8,762,19.05) rot=(0.57735,0.57735,0.57735;2.0944rad)
  LinkedObject = -> Extrude014
  Placement = pos=(50.8,762,19.05) rot=(0.57735,0.57735,0.57735;2.0944rad)
FEATURE [App::Link] Link023  label="BF_C001"
  LinkPlacement = pos=(800.1,800.1,19.05) rot=(0,0,1;3.14159rad)
  LinkedObject = -> Extrude013
  Placement = pos=(800.1,800.1,19.05) rot=(0,0,1;3.14159rad)
FEATURE [App::Link] Link024  label="BF_E001"
  LinkPlacement = pos=(400.05,406.4,196.85) rot=(0,-0.707107,0.707107;3.14159rad)
  LinkedObject = -> Extrude016
  Placement = pos=(400.05,406.4,196.85) rot=(0,-0.707107,0.707107;3.14159rad)
FEATURE [Part::Feature] Screw_w_Washer_A
  Placement = pos=(-0.7,25.4,37.3) rot=(0,1,0;1.5708rad)
  shape: bbox 38.1 x 15.88 x 15.88 mm, 35 faces (baked)
FEATURE [App::Link] Link025  label="Screw_w_Washer_A001"
  LinkPlacement = pos=(-0.774999,736.6,37.3) rot=(0,1,0;1.5708rad)
  LinkedObject = -> Screw_w_Washer_A
  Placement = pos=(-0.774999,736.6,37.3) rot=(0,1,0;1.5708rad)
FEATURE [App::Link] Link026  label="Screw_w_Washer_A002"
  LinkPlacement = pos=(-0.793745,508,38.1) rot=(0,1,0;1.5708rad)
  LinkedObject = -> Screw_w_Washer_A
  Placement = pos=(-0.793745,508,38.1) rot=(0,1,0;1.5708rad)
FEATURE [App::Link] Link027  label="Screw_w_Washer_A003"
  LinkPlacement = pos=(-0.793745,254,38.1) rot=(0,1,0;1.5708rad)
  LinkedObject = -> Screw_w_Washer_A
  Placement = pos=(-0.793745,254,38.1) rot=(0,1,0;1.5708rad)
FEATURE [App::Link] Link028  label="Screw_w_Washer_A004"
  LinkPlacement = pos=(-0.793742,781.05,63.5) rot=(0,1,0;1.5708rad)
  LinkedObject = -> Screw_w_Washer_A
  Placement = pos=(-0.793742,781.05,63.5) rot=(0,1,0;1.5708rad)
FEATURE [App::Link] Link029  label="Screw_w_Washer_A005"
  LinkPlacement = pos=(-0.793729,781.05,177.8) rot=(0,1,0;1.5708rad)
  LinkedObject = -> Screw_w_Washer_A
  Placement = pos=(-0.793729,781.05,177.8) rot=(0,1,0;1.5708rad)
FEATURE [App::Link] Link030  label="Screw_w_Washer_A006"
  LinkPlacement = pos=(31.75,813.594,38.1) rot=(1,0,0;1.5708rad)
  LinkedObject = -> Screw_w_Washer_A
  Placement = pos=(31.75,813.594,38.1) rot=(1,0,0;1.5708rad)
FEATURE [App::Link] Link031  label="Screw_w_Washer_A007"
  LinkPlacement = pos=(31.75,813.594,139.7) rot=(1,0,0;1.5708rad)
  LinkedObject = -> Screw_w_Washer_A
  Placement = pos=(31.75,813.594,139.7) rot=(1,0,0;1.5708rad)
FEATURE [App::Link] Link032  label="Screw_w_Washer_A008"
  LinkPlacement = pos=(95.25,813.6,177.8) rot=(1,0,0;1.5708rad)
  LinkedObject = -> Screw_w_Washer_A
  Placement = pos=(95.25,813.6,177.8) rot=(1,0,0;1.5708rad)
FEATURE [App::Link] Link033  label="Screw_w_Washer_A009"
  LinkPlacement = pos=(-1.58748,38.1,177.8) rot=(0,1,0;1.5708rad)
  LinkedObject = -> Screw_w_Washer_A
  Placement = pos=(-1.58748,38.1,177.8) rot=(0,1,0;1.5708rad)
FEATURE [App::Link] Link034  label="Screw_w_Washer_A010"
  LinkPlacement = pos=(-0.793758,279.4,177.8) rot=(0,1,0;1.5708rad)
  LinkedObject = -> Screw_w_Washer_A
  Placement = pos=(-0.793758,279.4,177.8) rot=(0,1,0;1.5708rad)
FEATURE [App::Link] Link035  label="Screw_w_Washer_A011"
  LinkPlacement = pos=(-0.793729,533.4,177.8) rot=(0,1,0;1.5708rad)
  LinkedObject = -> Screw_w_Washer_A
  Placement = pos=(-0.793729,533.4,177.8) rot=(0,1,0;1.5708rad)
FEATURE [App::Link] Link036  label="Screw_w_Washer_A012"
  LinkPlacement = pos=(31.7501,25.4,210.344) rot=(0.707107,0.707107,0;3.14159rad)
  LinkedObject = -> Screw_w_Washer_A
  Placement = pos=(31.7501,25.4,210.344) rot=(0.707107,0.707107,0;3.14159rad)
FEATURE [App::Link] Link037  label="Screw_w_Washer_A013"
  LinkPlacement = pos=(69.85,781.05,210.344) rot=(0,1,0;3.14159rad)
  LinkedObject = -> Screw_w_Washer_A
  Placement = pos=(69.85,781.05,210.344) rot=(0,1,0;3.14159rad)
FEATURE [App::Link] Link038  label="Screw_w_Washer_A014"
  LinkPlacement = pos=(31.75,755.65,210.344) rot=(0,1,0;3.14159rad)
  LinkedObject = -> Screw_w_Washer_A
  Placement = pos=(31.75,755.65,210.344) rot=(0,1,0;3.14159rad)
FEATURE [App::Link] Link039  label="Screw_w_Washer_A015"
  LinkPlacement = pos=(31.75,393.7,210.344) rot=(0,1,0;3.14159rad)
  LinkedObject = -> Screw_w_Washer_A
  Placement = pos=(31.75,393.7,210.344) rot=(0,1,0;3.14159rad)
FEATURE [App::Link] Link040  label="Screw_w_Washer_A016"
  LinkPlacement = pos=(31.75,196.85,210.344) rot=(0,1,0;3.14159rad)
  LinkedObject = -> Screw_w_Washer_A
  Placement = pos=(31.75,196.85,210.344) rot=(0,1,0;3.14159rad)
FEATURE [App::Link] Link041  label="Screw_w_Washer_A017"
  LinkPlacement = pos=(31.75,584.201,210.344) rot=(0,1,0;3.14159rad)
  LinkedObject = -> Screw_w_Washer_A
  Placement = pos=(31.75,584.201,210.344) rot=(0,1,0;3.14159rad)
FEATURE [App::Link] Link042  label="Screw_w_Washer_A018"
  LinkPlacement = pos=(742.95,781.05,210.344) rot=(0,1,0;3.14159rad)
  LinkedObject = -> Screw_w_Washer_A
  Placement = pos=(742.95,781.05,210.344) rot=(0,1,0;3.14159rad)
FEATURE [App::Link] Link043  label="Screw_w_Washer_A019"
  LinkPlacement = pos=(533.4,781.05,210.344) rot=(1,0,0;3.14159rad)
  LinkedObject = -> Screw_w_Washer_A
  Placement = pos=(533.4,781.05,210.344) rot=(1,0,0;3.14159rad)
FEATURE [App::Link] Link044  label="Screw_w_Washer_A020"
  LinkPlacement = pos=(279.4,781.05,210.344) rot=(0,1,0;3.14159rad)
  LinkedObject = -> Screw_w_Washer_A
  Placement = pos=(279.4,781.05,210.344) rot=(0,1,0;3.14159rad)
FEATURE [App::Link] Link045  label="Screw_w_Washer_A021"
  LinkPlacement = pos=(781.05,25.4002,210.344) rot=(0,1,0;3.14159rad)
  LinkedObject = -> Screw_w_Washer_A
  Placement = pos=(781.05,25.4002,210.344) rot=(0,1,0;3.14159rad)
FEATURE [App::Link] Link046  label="Screw_w_Washer_A022"
  LinkPlacement = pos=(781.05,755.65,210.344) rot=(0,1,0;3.14159rad)
  LinkedObject = -> Screw_w_Washer_A
  Placement = pos=(781.05,755.65,210.344) rot=(0,1,0;3.14159rad)
FEATURE [App::Link] Link047  label="Screw_w_Washer_A023"
  LinkPlacement = pos=(781.05,393.7,210.344) rot=(0,1,0;3.14159rad)
  LinkedObject = -> Screw_w_Washer_A
  Placement = pos=(781.05,393.7,210.344) rot=(0,1,0;3.14159rad)
FEATURE [App::Link] Link048  label="Screw_w_Washer_A024"
  LinkPlacement = pos=(781.05,584.201,210.344) rot=(0,1,0;3.14159rad)
  LinkedObject = -> Screw_w_Washer_A
  Placement = pos=(781.05,584.201,210.344) rot=(0,1,0;3.14159rad)
FEATURE [App::Link] Link049  label="Screw_w_Washer_A025"
  LinkPlacement = pos=(781.05,196.85,210.344) rot=(0,1,0;3.14159rad)
  LinkedObject = -> Screw_w_Washer_A
  Placement = pos=(781.05,196.85,210.344) rot=(0,1,0;3.14159rad)
FEATURE [App::Link] Link050  label="Screw_w_Washer_A026"
  LinkPlacement = pos=(431.8,19.0501,210.344) rot=(0,1,0;3.14159rad)
  LinkedObject = -> Screw_w_Washer_A
  Placement = pos=(431.8,19.0501,210.344) rot=(0,1,0;3.14159rad)
FEATURE [App::Link] Link051  label="Screw_w_Washer_A027"
  LinkPlacement = pos=(399.256,31.75,177.8) rot=(0,1,0;1.5708rad)
  LinkedObject = -> Screw_w_Washer_A
  Placement = pos=(399.256,31.75,177.8) rot=(0,1,0;1.5708rad)
FEATURE [App::Link] Link052  label="Screw_w_Washer_A028"
  LinkPlacement = pos=(381,387.35,210.344) rot=(0,1,0;3.14159rad)
  LinkedObject = -> Screw_w_Washer_A
  Placement = pos=(381,387.35,210.344) rot=(0,1,0;3.14159rad)
FEATURE [App::Link] Link053  label="Screw_w_Washer_A029"
  LinkPlacement = pos=(413.544,374.65,177.8) rot=(0,-1,0;1.5708rad)
  LinkedObject = -> Screw_w_Washer_A
  Placement = pos=(413.544,374.65,177.8) rot=(0,-1,0;1.5708rad)
FEATURE [App::Link] Link054  label="Screw_w_Washer_A030"
  LinkPlacement = pos=(414.338,225.425,41.2751) rot=(0,-1,0;1.5708rad)
  LinkedObject = -> Screw_w_Washer_A
  Placement = pos=(414.338,225.425,41.2751) rot=(0,-1,0;1.5708rad)
FEATURE [App::Link] Link055  label="Screw_w_Washer_A031"
  LinkPlacement = pos=(413.544,180.975,41.2751) rot=(0,-1,0;1.5708rad)
  LinkedObject = -> Screw_w_Washer_A
  Placement = pos=(413.544,180.975,41.2751) rot=(0,-1,0;1.5708rad)
FEATURE [App::Link] Link056  label="Screw_w_Washer_A032"
  LinkPlacement = pos=(723.9,813.601,177.8) rot=(1,0,0;1.5708rad)
  LinkedObject = -> Screw_w_Washer_A
  Placement = pos=(723.9,813.601,177.8) rot=(1,0,0;1.5708rad)
FEATURE [App::Link] Link057  label="Screw_w_Washer_A033"
  LinkPlacement = pos=(406.4,813.801,177.8) rot=(1,0,0;1.5708rad)
  LinkedObject = -> Screw_w_Washer_A
  Placement = pos=(406.4,813.801,177.8) rot=(1,0,0;1.5708rad)
FEATURE [App::Link] Link058  label="Screw_w_Washer_A034"
  LinkPlacement = pos=(406.4,813.8,38.1001) rot=(1,0,0;1.5708rad)
  LinkedObject = -> Screw_w_Washer_A
  Placement = pos=(406.4,813.8,38.1001) rot=(1,0,0;1.5708rad)
FEATURE [App::Link] Link059  label="Screw_w_Washer_A035"
  LinkPlacement = pos=(813.594,25.4001,38.1001) rot=(0,-1,0;1.5708rad)
  LinkedObject = -> Screw_w_Washer_A
  Placement = pos=(813.594,25.4001,38.1001) rot=(0,-1,0;1.5708rad)
FEATURE [App::Link] Link060  label="Screw_w_Washer_A036"
  LinkPlacement = pos=(813.594,254,38.1) rot=(0,-1,0;1.5708rad)
  LinkedObject = -> Screw_w_Washer_A
  Placement = pos=(813.594,254,38.1) rot=(0,-1,0;1.5708rad)
FEATURE [App::Link] Link061  label="Screw_w_Washer_A037"
  LinkPlacement = pos=(813.594,508,38.1001) rot=(0,-1,0;1.5708rad)
  LinkedObject = -> Screw_w_Washer_A
  Placement = pos=(813.594,508,38.1001) rot=(0,-1,0;1.5708rad)
FEATURE [App::Link] Link062  label="Screw_w_Washer_A038"
  LinkPlacement = pos=(813.594,736.6,38.1001) rot=(0,-1,0;1.5708rad)
  LinkedObject = -> Screw_w_Washer_A
  Placement = pos=(813.594,736.6,38.1001) rot=(0,-1,0;1.5708rad)
FEATURE [App::Link] Link063  label="Screw_w_Washer_A039"
  LinkPlacement = pos=(723.9,813.8,38.1001) rot=(1,0,0;1.5708rad)
  LinkedObject = -> Screw_w_Washer_A
  Placement = pos=(723.9,813.8,38.1001) rot=(1,0,0;1.5708rad)
FEATURE [App::Link] Link064  label="Screw_w_Washer_A040"
  LinkPlacement = pos=(781.05,813.594,38.1001) rot=(1,0,0;1.5708rad)
  LinkedObject = -> Screw_w_Washer_A
  Placement = pos=(781.05,813.594,38.1001) rot=(1,0,0;1.5708rad)
FEATURE [App::Link] Link065  label="Screw_w_Washer_A041"
  LinkPlacement = pos=(781.05,813.8,139.7) rot=(1,0,0;1.5708rad)
  LinkedObject = -> Screw_w_Washer_A
  Placement = pos=(781.05,813.8,139.7) rot=(1,0,0;1.5708rad)
FEATURE [App::Link] Link066  label="Screw_w_Washer_A042"
  LinkPlacement = pos=(813.594,38.1001,177.8) rot=(0,-1,0;1.5708rad)
  LinkedObject = -> Screw_w_Washer_A
  Placement = pos=(813.594,38.1001,177.8) rot=(0,-1,0;1.5708rad)
FEATURE [App::Link] Link067  label="Screw_w_Washer_A043"
  LinkPlacement = pos=(813.594,279.4,177.8) rot=(0,-1,0;1.5708rad)
  LinkedObject = -> Screw_w_Washer_A
  Placement = pos=(813.594,279.4,177.8) rot=(0,-1,0;1.5708rad)
FEATURE [App::Link] Link068  label="Screw_w_Washer_A044"
  LinkPlacement = pos=(813.594,533.4,177.8) rot=(0,-1,0;1.5708rad)
  LinkedObject = -> Screw_w_Washer_A
  Placement = pos=(813.594,533.4,177.8) rot=(0,-1,0;1.5708rad)
FEATURE [App::Link] Link069  label="Screw_w_Washer_A045"
  LinkPlacement = pos=(813.594,781.05,177.8) rot=(0,-1,0;1.5708rad)
  LinkedObject = -> Screw_w_Washer_A
  Placement = pos=(813.594,781.05,177.8) rot=(0,-1,0;1.5708rad)
FEATURE [App::Link] Link070  label="Screw_w_Washer_A046"
  LinkPlacement = pos=(813.5,781.05,63.5001) rot=(0,-1,0;1.5708rad)
  LinkedObject = -> Screw_w_Washer_A
  Placement = pos=(813.5,781.05,63.5001) rot=(0,-1,0;1.5708rad)
FEATURE [Part::Cylinder] Cylinder
  Angle = 360
  AttacherType = Attacher::AttachEngine3D
  FirstAngle = 0
  Height = 50.8
  Placement = pos=(381,203.2,16.6687) rot=(0,0,1;0rad)
  Radius = 3.96875
  SecondAngle = 0
FEATURE [Part::Cut] Cut  label="Baffle_Anchor_A"
  Base = -> Extrude017
  Tool = -> Cylinder
FEATURE [Part::Feature] User_Library_t_nut_scaleable_M6  label="T-Nut_1/4"
  Placement = pos=(381,203.2,64.7937) rot=(-1,0,0;1.5708rad)
  shape: bbox 18 x 18 x 9 mm, 45 faces (baked)
FEATURE [App::Link] Link071  label="Cylinder001"
  LinkPlacement = pos=(31.75,50.8,12.7) rot=(0,0,1;0rad)
  LinkedObject = -> Cylinder
  Placement = pos=(31.75,50.8,12.7) rot=(0,0,1;0rad)
FEATURE [App::Link] Link072  label="Cylinder002"
  LinkPlacement = pos=(31.75,381,12.7) rot=(0,0,1;0rad)
  LinkedObject = -> Cylinder
  Placement = pos=(31.75,381,12.7) rot=(0,0,1;0rad)
FEATURE [App::Link] Link073  label="Cylinder003"
  LinkPlacement = pos=(31.75,711.201,12.7) rot=(0,0,1;0rad)
  LinkedObject = -> Cylinder
  Placement = pos=(31.75,711.201,12.7) rot=(0,0,1;0rad)
FEATURE [Part::Cut] Cut001
  Base = -> Extrude015
  Tool = -> Link071
FEATURE [Part::Cut] Cut002
  Base = -> Cut001
  Tool = -> Link072
FEATURE [Part::Cut] Cut003  label="Baffle_Frame_D"
  Base = -> Cut002
  Tool = -> Link073
FEATURE [App::Link] Link074  label="Baffle_Frame_D001"
  LinkPlacement = pos=(749.3,-8.93235e-05,0) rot=(0,0,1;0rad)
  LinkedObject = -> Cut003
  Placement = pos=(749.3,-8.93235e-05,0) rot=(0,0,1;0rad)
FEATURE [App::Link] Link075  label="T-Nut_1/005"
  LinkPlacement = pos=(31.75,50.8,58.45) rot=(-1,0,0;1.5708rad)
  LinkedObject = -> User_Library_t_nut_scaleable_M6
  Placement = pos=(31.75,50.8,58.45) rot=(-1,0,0;1.5708rad)
FEATURE [App::Link] Link076  label="T-Nut_1/006"
  LinkPlacement = pos=(31.75,381,58.35) rot=(-1,0,0;1.5708rad)
  LinkedObject = -> User_Library_t_nut_scaleable_M6
  Placement = pos=(31.75,381,58.35) rot=(-1,0,0;1.5708rad)
FEATURE [App::Link] Link077  label="T-Nut_1/007"
  LinkPlacement = pos=(31.75,711.2,58.4) rot=(-1,0,0;1.5708rad)
  LinkedObject = -> User_Library_t_nut_scaleable_M6
  Placement = pos=(31.75,711.2,58.4) rot=(-1,0,0;1.5708rad)
FEATURE [App::Link] Link078  label="T-Nut_1/008"
  LinkPlacement = pos=(781.051,50.8,58.4501) rot=(-1,0,0;1.5708rad)
  LinkedObject = -> User_Library_t_nut_scaleable_M6
  Placement = pos=(781.051,50.8,58.4501) rot=(-1,0,0;1.5708rad)
FEATURE [App::Link] Link079  label="T-Nut_1/009"
  LinkPlacement = pos=(781.05,381,58.3502) rot=(-1,0,0;1.5708rad)
  LinkedObject = -> User_Library_t_nut_scaleable_M6
  Placement = pos=(781.05,381,58.3502) rot=(-1,0,0;1.5708rad)
FEATURE [App::Link] Link080  label="T-Nut_1/010"
  LinkPlacement = pos=(781.051,711.2,58.4501) rot=(-1,0,0;1.5708rad)
  LinkedObject = -> User_Library_t_nut_scaleable_M6
  Placement = pos=(781.051,711.2,58.4501) rot=(-1,0,0;1.5708rad)
FEATURE [App::Link] Link081  label="Cylinder004"
  LinkPlacement = pos=(254,781.05,12.7) rot=(0,0,1;0rad)
  LinkedObject = -> Cylinder
  Placement = pos=(254,781.05,12.7) rot=(0,0,1;0rad)
FEATURE [App::Link] Link082  label="Cylinder005"
  LinkPlacement = pos=(558.8,781.05,12.7) rot=(0,0,1;0rad)
  LinkedObject = -> Cylinder
  Placement = pos=(558.8,781.05,12.7) rot=(0,0,1;0rad)
FEATURE [Part::Cut] Cut004
  Base = -> Link022
  Tool = -> Link081
FEATURE [Part::Cut] Cut005  label="Baffle_Frame_B"
  Base = -> Cut004
  Tool = -> Link082
FEATURE [App::Link] Link083  label="T-Nut_1/011"
  LinkPlacement = pos=(254,781.05,58.4501) rot=(-1,0,0;1.5708rad)
  LinkedObject = -> User_Library_t_nut_scaleable_M6
  Placement = pos=(254,781.05,58.4501) rot=(-1,0,0;1.5708rad)
FEATURE [App::Link] Link084  label="T-Nut_1/012"
  LinkPlacement = pos=(558.8,781.05,58.4501) rot=(-1,0,0;1.5708rad)
  LinkedObject = -> User_Library_t_nut_scaleable_M6
  Placement = pos=(558.8,781.05,58.4501) rot=(-1,0,0;1.5708rad)
FEATURE [App::Link] Link085  label="Screw_w_Washer_A047"
  LinkPlacement = pos=(95.25,813.594,38.1002) rot=(1,0,0;1.5708rad)
  LinkedObject = -> Screw_w_Washer_A
  Placement = pos=(95.25,813.594,38.1002) rot=(1,0,0;1.5708rad)
FEATURE [App::Link] Link  label="IF_A001"
  LinkPlacement = pos=(19.05,2.707e-13,2.27094e-06) rot=(-1,0,0;1.5708rad)
  LinkedObject = -> Extrude006
  Placement = pos=(19.05,2.707e-13,2.27094e-06) rot=(-1,0,0;1.5708rad)
FEATURE [App::LinkGroup] LinkGroup002  label="Inlet_Wall_LinkGroup"
  ElementList = -> [Extrude004,Extrude006,Link,Screw_w_Washer_B,Link001,Link002,Link003,Link004,Link005,LinkGroup,LinkGroup001]
  LinkMode = 0
  Placement = pos=(0,-7.62939e-06,-0.000183105) rot=(0,0,1;0rad)
FEATURE [Part::Feature] Screw_w_Washer_C001
  Placement = pos=(31.75,50.8,-393.1) rot=(0,0,1;0rad)
  shape: bbox 25.4 x 25.4 x 106.1 mm, 32 faces (baked)
FEATURE [App::Link] Link086  label="Screw_w_Washer_C002"
  LinkPlacement = pos=(31.75,381,-393.1) rot=(0,0,1;0rad)
  LinkedObject = -> Screw_w_Washer_C001
  Placement = pos=(31.75,381,-393.1) rot=(0,0,1;0rad)
FEATURE [App::Link] Link087  label="Screw_w_Washer_C003"
  LinkPlacement = pos=(31.75,711.2,-393.1) rot=(0,0,1;0rad)
  LinkedObject = -> Screw_w_Washer_C001
  Placement = pos=(31.75,711.2,-393.1) rot=(0,0,1;0rad)
FEATURE [App::Link] Link088  label="Screw_w_Washer_C004"
  LinkTransform = true
  LinkedObject = -> Screw_w_Washer_C001
FEATURE [App::Link] Link089  label="Screw_w_Washer_C005"
  LinkTransform = true
  LinkedObject = -> Link086
FEATURE [App::Link] Link090  label="Screw_w_Washer_C006"
  LinkTransform = true
  LinkedObject = -> Link087
FEATURE [App::LinkGroup] LinkGroup003
  ElementList = -> [Link088,Link089,Link090]
  LinkMode = 1
  Placement = pos=(749.3,-9.15527e-05,-1.52588e-05) rot=(0,0,1;0rad)
FEATURE [Part::Feature] Screw_w_Washer_D
  Placement = pos=(381,203.2,-355) rot=(0,0,1;0rad)
  shape: bbox 25.4 x 25.4 x 67.97 mm, 30 faces (baked)
FEATURE [App::Link] Link091  label="Screw_w_Washer_D001"
  LinkPlacement = pos=(254,781.05,-355) rot=(0,0,1;0rad)
  LinkedObject = -> Screw_w_Washer_D
  Placement = pos=(254,781.05,-355) rot=(0,0,1;0rad)
FEATURE [App::Link] Link092  label="Screw_w_Washer_D002"
  LinkPlacement = pos=(558.8,781.05,-355.1) rot=(0,0,1;0rad)
  LinkedObject = -> Screw_w_Washer_D
  Placement = pos=(558.8,781.05,-355.1) rot=(0,0,1;0rad)
FEATURE [App::LinkGroup] LinkGroup004  label="LinkGroup_Baffle_Anchor_Screws"
  ElementList = -> [Screw_w_Washer_C001,Link086,Link087,LinkGroup003,Screw_w_Washer_D,Link091,Link092]
  LinkMode = 0
  Placement = pos=(-0.00012207,-0.00012207,355.6) rot=(0,0,1;0rad)
FEATURE [App::LinkGroup] LinkGroup005  label="LinkGroup_Baffle_Box"
  ElementList = -> [Extrude,Extrude008,Extrude009,Extrude010,Extrude012,Extrude013,Extrude014,Extrude016,Link020,Link021,Link023,Link024,Screw_w_Washer_A,Link025,Link026,Link027,Link028,Link029,Link030,Link031,Link032,Link033,Link034,Link035,Link036,Link037,Link038,Link039,Link040,Link041,Link042,Link043,Link044,Link045,Link046,Link047,Link048,Link049,Link050,Link051,Link052,Link053,Link054,Link055,Link056,Link057,+27 more]
  LinkMode = 0
FEATURE [App::Link] Link093  label="LinkGroup_Baffle_Box_2"
  LinkPlacement = pos=(812.8,0.000186974,-1390.65) rot=(0,1,0;3.14159rad)
  LinkedObject = -> LinkGroup005
  Placement = pos=(812.8,0.000186974,-1390.65) rot=(0,1,0;3.14159rad)
FEATURE [App::Link] Link094  label="LinkGroup_Baffle_Anchor_Screws_2"
  LinkPlacement = pos=(812.8,-0.000111276,-1746.25) rot=(0,1,0;3.14159rad)
  LinkedObject = -> LinkGroup004
  Placement = pos=(812.8,-0.000111276,-1746.25) rot=(0,1,0;3.14159rad)
FEATURE [Sketcher::SketchObject] Sketch018  label="Sketch_2x2_rail007"
  FullyConstrained = false
  sketch-geometry (8):
    g0: LineSegment StartX=0 StartY=34.925 StartZ=0 EndX=0 EndY=3.175 EndZ=0
    g1: ArcOfCircle CenterX=3.175 CenterY=34.925 CenterZ=0 NormalX=0 NormalY=0 NormalZ=1 AngleXU=0 Radius=3.175 StartAngle=1.5708 EndAngle=3.14159
    g2: LineSegment StartX=3.175 StartY=38.1 StartZ=0 EndX=34.925 EndY=38.1 EndZ=0
    g3: ArcOfCircle CenterX=34.925 CenterY=34.925 CenterZ=0 NormalX=0 NormalY=0 NormalZ=1 AngleXU=0 Radius=3.175 StartAngle=4e-16 EndAngle=1.5708
    g4: LineSegment StartX=38.1 StartY=34.925 StartZ=0 EndX=38.1 EndY=3.175 EndZ=0
    g5: ArcOfCircle CenterX=34.925 CenterY=3.175 CenterZ=0 NormalX=0 NormalY=0 NormalZ=1 AngleXU=0 Radius=3.175 StartAngle=4.71239 EndAngle=6.28319
    g6: LineSegment StartX=34.925 StartY=0 StartZ=0 EndX=3.175 EndY=0 EndZ=0
    g7: ArcOfCircle CenterX=3.175 CenterY=3.175 CenterZ=0 NormalX=0 NormalY=0 NormalZ=1 AngleXU=0 Radius=3.175 StartAngle=3.14159 EndAngle=4.71239
  constraints (22):
    c: Vertical(g0)
    c: Tangent(g0,g1) = -1.5708
    c: Radius(g1) = 3.175
    c: Angle(g1) = 1.5708
    c: Coincident(g2,g1)
    c: Horizontal(g2)
    c: Tangent(g2,g3) = 1.5708
    c: Coincident(g4,g3)
    c: Vertical(g4)
    c: Tangent(g5,g4) = 1.5708
    c: Horizontal(g6)
    c: Tangent(g6,g5) = 1.5708
    c: Tangent(g7,g6) = 1.5708
    c: Tangent(g7,g0) = -1.5708
    c: Equal(g1,g7)
    c: Equal(g7,g3)
    c: Equal(g2,g0)
    c: Equal(g0,g6)
    c: Equal(g6,g4)
    c: PointOnObject(g-1,g0)
    c: PointOnObject(g6,g-1)
    c: DistanceX(g0,g4) = 38.1
FEATURE [App::Link] Link095  label="IF_A002"
  LinkPlacement = pos=(19.05,1.929e-13,1.61828e-06) rot=(0.57735,0.57735,0.57735;4.18879rad)
  LinkedObject = -> Extrude018
  Placement = pos=(19.05,1.929e-13,1.61828e-06) rot=(0.57735,0.57735,0.57735;4.18879rad)
FEATURE [Sketcher::SketchObject] Sketch003  label="Sketch_C_Outlet_Wall"
  FullyConstrained = false
  sketch-geometry (10):
    g0: LineSegment StartX=812.8 StartY=812.8 StartZ=0 EndX=0 EndY=812.8 EndZ=0
    g1: LineSegment StartX=0 StartY=812.8 StartZ=0 EndX=0 EndY=0 EndZ=0
    g2: LineSegment StartX=0 StartY=0 StartZ=0 EndX=431.8 EndY=0 EndZ=0
    g3: LineSegment StartX=812.8 StartY=0 StartZ=0 EndX=812.8 EndY=812.8 EndZ=0
    g4: LineSegment StartX=812.8 StartY=0 StartZ=0 EndX=736.6 EndY=0 EndZ=0
    g5: LineSegment StartX=482.6 StartY=304.8 StartZ=0 EndX=685.8 EndY=304.8 EndZ=0
    g6: LineSegment StartX=431.8 StartY=0 StartZ=0 EndX=431.8 EndY=254 EndZ=0
    g7: LineSegment StartX=736.6 StartY=0 StartZ=0 EndX=736.6 EndY=254 EndZ=0
    g8: ArcOfCircle CenterX=482.6 CenterY=254 CenterZ=0 NormalX=0 NormalY=0 NormalZ=1 AngleXU=0 Radius=50.8 StartAngle=1.5708 EndAngle=3.14159
    g9: ArcOfCircle CenterX=685.8 CenterY=254 CenterZ=0 NormalX=0 NormalY=0 NormalZ=1 AngleXU=0 Radius=50.8 StartAngle=0 EndAngle=1.5708
  constraints (32):
    c: Coincident(g0,g1)
    c: Coincident(g2,g1)
    c: Coincident(g3,g0)
    c: DistanceX(g1) = 0
    c: DistanceY(g1) = 0
    c: Vertical(g0,g1)
    c: Vertical(g0,g3)
    c: Horizontal(g0,g0)
    c: DistanceY(g1,g0) = 812.8
    c: DistanceX(g0,g0) = 812.8
    c: Horizontal(g2)
    c: Coincident(g4,g3)
    c: PointOnObject(g4,g-1)
    c: Horizontal(g4)
    c: Horizontal(g5)
    c: DistanceX(g2,g4) = 304.8
    c: DistanceX(g4,g4) = 76.2
    c: DistanceY(g2,g5) = 304.8
    c: Coincident(g6,g2)
    c: Vertical(g6)
    c: Coincident(g7,g4)
    c: Vertical(g7)
    c: Equal(g6,g7)
    c: Coincident(g8,g5)
    c: Coincident(g8,g6)
    c: Coincident(g9,g5)
    c: Coincident(g9,g7)
    c: Horizontal(g6,g8)
    c: Vertical(g8,g5)
    c: Horizontal(g9,g7)
    c: Vertical(g9,g5)
    c: DistanceX(g6,g8) = 50.8
FEATURE [Part::Extrusion] Extrude003  label="Part_C_Outlet_Wall"
  Base = -> Sketch003
  Dir = (0,0,1)
  DirMode = 2
  FaceMakerClass = Part::FaceMakerBullseye
  LengthFwd = 19.05
  LengthRev = 0
  Placement = pos=(812.8,0,1e-13) rot=(0,1,0;3.14159rad)
  Solid = true
  Symmetric = false
FEATURE [Part::Extrusion] Extrude018  label="IF_A003"
  Base = -> Sketch018
  Dir = (0,0,1)
  DirMode = 2
  FaceMakerClass = Part::FaceMakerBullseye
  LengthFwd = 762
  LengthRev = 0
  Placement = pos=(755.65,-4e-15,6e-15) rot=(0.57735,0.57735,0.57735;4.18879rad)
  Solid = true
  Symmetric = false
FEATURE [Part::Feature] Screw_w_Washer_B001  label="Screw_w_Washer_B020"
  Placement = pos=(38.1,25.4,-19.05) rot=(0,0,1;0rad)
  shape: bbox 15.88 x 15.88 x 50.8 mm, 35 faces (baked)
FEATURE [App::Link] Link096  label="Screw_w_Washer_B021"
  LinkPlacement = pos=(38.1,736.601,-19.05) rot=(0,0,1;0rad)
  LinkedObject = -> Screw_w_Washer_B001
  Placement = pos=(38.1,736.601,-19.05) rot=(0,0,1;0rad)
FEATURE [App::Link] Link097  label="Screw_w_Washer_B022"
  LinkPlacement = pos=(38.1,152.4,-19.05) rot=(0,0,1;0rad)
  LinkedObject = -> Screw_w_Washer_B001
  Placement = pos=(38.1,152.4,-19.05) rot=(0,0,1;0rad)
FEATURE [App::Link] Link098  label="Screw_w_Washer_B023"
  LinkPlacement = pos=(38.1,609.601,-19.05) rot=(0,0,1;0rad)
  LinkedObject = -> Screw_w_Washer_B001
  Placement = pos=(38.1,609.601,-19.05) rot=(0,0,1;0rad)
FEATURE [App::Link] Link099  label="Screw_w_Washer_B024"
  LinkPlacement = pos=(38.1,304.8,-19.05) rot=(0,0,1;0rad)
  LinkedObject = -> Screw_w_Washer_B001
  Placement = pos=(38.1,304.8,-19.05) rot=(0,0,1;0rad)
FEATURE [App::Link] Link100  label="Screw_w_Washer_B025"
  LinkPlacement = pos=(38.1,457.2,-19.05) rot=(0,0,1;0rad)
  LinkedObject = -> Screw_w_Washer_B001
  Placement = pos=(38.1,457.2,-19.05) rot=(0,0,1;0rad)
FEATURE [App::LinkGroup] LinkGroup006  label="Frame_Screws_A_LinkGroup"
  ElementList = -> [Screw_w_Washer_B001,Link096,Link097,Link098,Link099,Link100]
  LinkMode = 0
FEATURE [App::Link] Link101  label="Frame_Screws_A_LinkGroup001"
  LinkedObject = -> LinkGroup006
FEATURE [App::LinkGroup] LinkGroup007  label="Frame_Screws_A_LinkGroup_2"
  ElementList = -> [Link101]
  LinkMode = 1
  Placement = pos=(736.6,-9.15527e-05,0) rot=(0,0,1;0rad)
FEATURE [App::LinkGroup] LinkGroup008  label="Outlet_Wall_LinkGroup"
  ElementList = -> [Link095,Extrude003,Extrude018,LinkGroup006,LinkGroup007]
  LinkMode = 0
  Placement = pos=(-0.000367738,2.274e-13,-1390.65) rot=(0,1,0;0rad)
FEATURE [Sketcher::SketchObject] Sketch001  label="Sketch_B"
  FullyConstrained = false
  sketch-geometry (4):
    g0: LineSegment StartX=0 StartY=0 StartZ=0 EndX=914.4 EndY=0 EndZ=0
    g1: LineSegment StartX=914.4 StartY=0 StartZ=0 EndX=914.4 EndY=812.8 EndZ=0
    g2: LineSegment StartX=914.4 StartY=812.8 StartZ=0 EndX=0 EndY=812.8 EndZ=0
    g3: LineSegment StartX=0 StartY=812.8 StartZ=0 EndX=0 EndY=0 EndZ=0
  constraints (11):
    c: Coincident(g0,g1)
    c: Coincident(g1,g2)
    c: Coincident(g2,g3)
    c: Coincident(g3,g0)
    c: Horizontal(g0)
    c: Horizontal(g2)
    c: Vertical(g1)
    c: Vertical(g3)
    c: Distance(g0) = 914.4
    c: Distance(g1) = 812.8
    c: Coincident(g-1,g0)
FEATURE [Part::Extrusion] Extrude001  label="Part_B_Side_Wall_001"
  Base = -> Sketch001
  Dir = (0,0,1)
  DirMode = 2
  FaceMakerClass = Part::FaceMakerBullseye
  LengthFwd = 19.05
  LengthRev = 0
  Placement = pos=(812.8,7.6e-14,-914.4) rot=(0,-1,0;1.5708rad)
  Solid = true
  Symmetric = false
FEATURE [App::LinkGroup] LinkGroup009  label="Inlet_Box_LinkGroup"
  ElementList = -> [LinkGroup002,LinkGroup004,LinkGroup005]
  LinkMode = 0
  Placement = pos=(1.52588e-05,-9.25064e-05,0.000213623) rot=(0,0,1;0rad)
FEATURE [App::LinkGroup] LinkGroup010  label="Outlet_Box_LinkGroup"
  ElementList = -> [Link093,Link094,LinkGroup008]
  LinkMode = 0
  Placement = pos=(-3.05176e-05,-0.00012207,476.25) rot=(0,0,1;0rad)
FEATURE [App::Link] Link102  label="Part_B_Side_Wall_002"
  LinkPlacement = pos=(0,-9.095e-13,-9.095e-13) rot=(0,1,0;1.5708rad)
  LinkedObject = -> Extrude001
  Placement = pos=(0,-9.095e-13,-9.095e-13) rot=(0,1,0;1.5708rad)
FEATURE [Sketcher::SketchObject] Sketch019  label="Sketch_A"
  FullyConstrained = false
  sketch-geometry (4):
    g0: LineSegment StartX=0 StartY=0 StartZ=0 EndX=1016 EndY=0 EndZ=0
    g1: LineSegment StartX=1016 StartY=0 StartZ=0 EndX=1016 EndY=812.8 EndZ=0
    g2: LineSegment StartX=1016 StartY=812.8 StartZ=0 EndX=0 EndY=812.8 EndZ=0
    g3: LineSegment StartX=0 StartY=812.8 StartZ=0 EndX=0 EndY=0 EndZ=0
  constraints (11):
    c: Coincident(g0,g1)
    c: Coincident(g1,g2)
    c: Coincident(g2,g3)
    c: Coincident(g3,g0)
    c: Horizontal(g0)
    c: Horizontal(g2)
    c: Vertical(g1)
    c: Vertical(g3)
    c: Coincident(g0,g-1)
    c: Distance(g0) = 1016
    c: Distance(g1) = 812.8
FEATURE [Part::Extrusion] Extrude019  label="Part_A_Lid"
  Base = -> Sketch019
  Dir = (0,0,1)
  DirMode = 2
  FaceMakerClass = Part::FaceMakerBullseye
  LengthFwd = 19.05
  LengthRev = 0
  Placement = pos=(4.4e-14,-6.8e-14,-4.41e-13) rot=(0,0,1;0rad)
  Solid = true
  Symmetric = false
FEATURE [Sketcher::SketchObject] Sketch020  label="Sketch_2x2_rail008"
  FullyConstrained = false
  sketch-geometry (8):
    g0: LineSegment StartX=0 StartY=34.925 StartZ=0 EndX=0 EndY=3.175 EndZ=0
    g1: ArcOfCircle CenterX=3.175 CenterY=34.925 CenterZ=0 NormalX=0 NormalY=0 NormalZ=1 AngleXU=0 Radius=3.175 StartAngle=1.5708 EndAngle=3.14159
    g2: LineSegment StartX=3.175 StartY=38.1 StartZ=0 EndX=34.925 EndY=38.1 EndZ=0
    g3: ArcOfCircle CenterX=34.925 CenterY=34.925 CenterZ=0 NormalX=0 NormalY=0 NormalZ=1 AngleXU=0 Radius=3.175 StartAngle=1.2e-15 EndAngle=1.5708
    g4: LineSegment StartX=38.1 StartY=34.925 StartZ=0 EndX=38.1 EndY=3.175 EndZ=0
    g5: ArcOfCircle CenterX=34.925 CenterY=3.175 CenterZ=0 NormalX=0 NormalY=0 NormalZ=1 AngleXU=0 Radius=3.175 StartAngle=4.71239 EndAngle=6.28319
    g6: LineSegment StartX=34.925 StartY=0 StartZ=0 EndX=3.175 EndY=0 EndZ=0
    g7: ArcOfCircle CenterX=3.175 CenterY=3.175 CenterZ=0 NormalX=0 NormalY=0 NormalZ=1 AngleXU=0 Radius=3.175 StartAngle=3.14159 EndAngle=4.71239
  constraints (22):
    c: Vertical(g0)
    c: Tangent(g0,g1) = -1.5708
    c: Radius(g1) = 3.175
    c: Angle(g1) = 1.5708
    c: Coincident(g2,g1)
    c: Horizontal(g2)
    c: Tangent(g2,g3) = 1.5708
    c: Coincident(g4,g3)
    c: Vertical(g4)
    c: Tangent(g5,g4) = 1.5708
    c: Horizontal(g6)
    c: Tangent(g6,g5) = 1.5708
    c: Tangent(g7,g6) = 1.5708
    c: Tangent(g7,g0) = -1.5708
    c: Equal(g1,g7)
    c: Equal(g7,g3)
    c: Equal(g2,g0)
    c: Equal(g0,g6)
    c: Equal(g6,g4)
    c: PointOnObject(g-1,g0)
    c: PointOnObject(g6,g-1)
    c: DistanceX(g0,g4) = 38.1
FEATURE [Part::Extrusion] Extrude020  label="LF_A"
  Base = -> Sketch020
  Dir = (0,0,1)
  DirMode = 2
  FaceMakerClass = Part::FaceMakerBullseye
  LengthFwd = 914.4
  LengthRev = 0
  Placement = pos=(50.8,19.05,19.05) rot=(0.57735,0.57735,0.57735;2.0944rad)
  Solid = true
  Symmetric = false
FEATURE [Sketcher::SketchObject] Sketch021  label="Sketch_2x2_rail009"
  FullyConstrained = false
  sketch-geometry (8):
    g0: LineSegment StartX=0 StartY=34.925 StartZ=0 EndX=0 EndY=3.175 EndZ=0
    g1: ArcOfCircle CenterX=3.175 CenterY=34.925 CenterZ=0 NormalX=0 NormalY=0 NormalZ=1 AngleXU=0 Radius=3.175 StartAngle=1.5708 EndAngle=3.14159
    g2: LineSegment StartX=3.175 StartY=38.1 StartZ=0 EndX=34.925 EndY=38.1 EndZ=0
    g3: ArcOfCircle CenterX=34.925 CenterY=34.925 CenterZ=0 NormalX=0 NormalY=0 NormalZ=1 AngleXU=0 Radius=3.175 StartAngle=1.5e-15 EndAngle=1.5708
    g4: LineSegment StartX=38.1 StartY=34.925 StartZ=0 EndX=38.1 EndY=3.175 EndZ=0
    g5: ArcOfCircle CenterX=34.925 CenterY=3.175 CenterZ=0 NormalX=0 NormalY=0 NormalZ=1 AngleXU=0 Radius=3.175 StartAngle=4.71239 EndAngle=6.28319
    g6: LineSegment StartX=34.925 StartY=4e-16 StartZ=0 EndX=3.175 EndY=4e-16 EndZ=0
    g7: ArcOfCircle CenterX=3.175 CenterY=3.175 CenterZ=0 NormalX=0 NormalY=0 NormalZ=1 AngleXU=0 Radius=3.175 StartAngle=3.14159 EndAngle=4.71239
  constraints (22):
    c: Vertical(g0)
    c: Tangent(g0,g1) = -1.5708
    c: Radius(g1) = 3.175
    c: Angle(g1) = 1.5708
    c: Coincident(g2,g1)
    c: Horizontal(g2)
    c: Tangent(g2,g3) = 1.5708
    c: Coincident(g4,g3)
    c: Vertical(g4)
    c: Tangent(g5,g4) = 1.5708
    c: Horizontal(g6)
    c: Tangent(g6,g5) = 1.5708
    c: Tangent(g7,g6) = 1.5708
    c: Tangent(g7,g0) = -1.5708
    c: Equal(g1,g7)
    c: Equal(g7,g3)
    c: Equal(g2,g0)
    c: Equal(g0,g6)
    c: Equal(g6,g4)
    c: PointOnObject(g-1,g0)
    c: PointOnObject(g6,g-1)
    c: DistanceX(g0,g4) = 38.1
FEATURE [Part::Extrusion] Extrude021  label="LF_B"
  Base = -> Sketch021
  Dir = (0,0,1)
  DirMode = 2
  FaceMakerClass = Part::FaceMakerBullseye
  LengthFwd = 698.5
  LengthRev = 0
  Placement = pos=(965.2,57.15,19.05) rot=(0,0.707107,0.707107;3.14159rad)
  Solid = true
  Symmetric = false
FEATURE [App::Link] Link103  label="LF_A001"
  LinkPlacement = pos=(50.8005,793.75,19.0502) rot=(0.707107,0,0.707107;3.14159rad)
  LinkedObject = -> Extrude020
  Placement = pos=(50.8005,793.75,19.0502) rot=(0.707107,0,0.707107;3.14159rad)
FEATURE [App::Link] Link104  label="LF_B001"
  LinkPlacement = pos=(50.8,57.1502,19.0496) rot=(-0.57735,-0.57735,-0.57735;2.0944rad)
  LinkedObject = -> Extrude021
  Placement = pos=(50.8,57.1502,19.0496) rot=(-0.57735,-0.57735,-0.57735;2.0944rad)
FEATURE [Part::Feature] Screw_w_Washer_B002  label="Screw_w_Washer_B026"
  Placement = pos=(69.85,82.55,1.48e-13) rot=(0,0,1;0rad)
  shape: bbox 15.88 x 15.88 x 50.8 mm, 35 faces (baked)
FEATURE [App::Link] Link105  label="Screw_w_Washer_B027"
  LinkPlacement = pos=(69.85,730.249,0.000169754) rot=(0,0,-1;1.5708rad)
  LinkedObject = -> Screw_w_Washer_B002
  Placement = pos=(69.85,730.249,0.000169754) rot=(0,0,-1;1.5708rad)
FEATURE [App::Link] Link106  label="Screw_w_Washer_B028"
  LinkPlacement = pos=(69.8501,209.55,0.000109673) rot=(0,0,1;0rad)
  LinkedObject = -> Screw_w_Washer_B002
  Placement = pos=(69.8501,209.55,0.000109673) rot=(0,0,1;0rad)
FEATURE [App::Link] Link107  label="Screw_w_Washer_B029"
  LinkPlacement = pos=(69.85,336.55,0) rot=(0,0,1;0rad)
  LinkedObject = -> Screw_w_Washer_B002
  Placement = pos=(69.85,336.55,0) rot=(0,0,1;0rad)
FEATURE [App::Link] Link108  label="Screw_w_Washer_B030"
  LinkPlacement = pos=(69.85,603.25,0) rot=(0,0,1;0rad)
  LinkedObject = -> Screw_w_Washer_B002
  Placement = pos=(69.85,603.25,0) rot=(0,0,1;0rad)
FEATURE [App::Link] Link109  label="Screw_w_Washer_B031"
  LinkPlacement = pos=(69.85,476.25,0) rot=(0,0,1;0rad)
  LinkedObject = -> Screw_w_Washer_B002
  Placement = pos=(69.85,476.25,0) rot=(0,0,1;0rad)
FEATURE [App::Link] Link110  label="Screw_w_Washer_B032"
  LinkTransform = true
  LinkedObject = -> Screw_w_Washer_B002
FEATURE [App::Link] Link111  label="Screw_w_Washer_B033"
  LinkTransform = true
  LinkedObject = -> Link105
FEATURE [App::Link] Link112  label="Screw_w_Washer_B034"
  LinkTransform = true
  LinkedObject = -> Link106
FEATURE [App::Link] Link113  label="Screw_w_Washer_B035"
  LinkTransform = true
  LinkedObject = -> Link107
FEATURE [App::Link] Link114  label="Screw_w_Washer_B036"
  LinkTransform = true
  LinkedObject = -> Link108
FEATURE [App::Link] Link115  label="Screw_w_Washer_B037"
  LinkTransform = true
  LinkedObject = -> Link109
FEATURE [App::LinkGroup] LinkGroup011
  ElementList = -> [Link110,Link111,Link112,Link113,Link114,Link115]
  LinkMode = 1
  Placement = pos=(876.301,3.05176e-05,-7.7486e-07) rot=(0,0,1;0rad)
FEATURE [App::Link] Link116  label="Screw_w_Washer_B038"
  LinkPlacement = pos=(76.2,38.1,0) rot=(0,0,1;0rad)
  LinkedObject = -> Screw_w_Washer_B002
  Placement = pos=(76.2,38.1,0) rot=(0,0,1;0rad)
FEATURE [App::Link] Link117  label="Screw_w_Washer_B039"
  LinkPlacement = pos=(939.8,38.0999,0) rot=(0,0,1;0rad)
  LinkedObject = -> Screw_w_Washer_B002
  Placement = pos=(939.8,38.0999,0) rot=(0,0,1;0rad)
FEATURE [App::Link] Link118  label="Screw_w_Washer_B040"
  LinkPlacement = pos=(203.2,38.1,0) rot=(0,0,1;0rad)
  LinkedObject = -> Screw_w_Washer_B002
  Placement = pos=(203.2,38.1,0) rot=(0,0,1;0rad)
FEATURE [App::Link] Link119  label="Screw_w_Washer_B041"
  LinkPlacement = pos=(812.8,38.0999,0) rot=(0,0,1;0rad)
  LinkedObject = -> Screw_w_Washer_B002
  Placement = pos=(812.8,38.0999,0) rot=(0,0,1;0rad)
FEATURE [App::Link] Link120  label="Screw_w_Washer_B042"
  LinkPlacement = pos=(355.6,38.1,0) rot=(0,0,1;0rad)
  LinkedObject = -> Screw_w_Washer_B002
  Placement = pos=(355.6,38.1,0) rot=(0,0,1;0rad)
FEATURE [App::Link] Link121  label="Screw_w_Washer_B043"
  LinkPlacement = pos=(660.4,38.0999,0) rot=(0,0,1;0rad)
  LinkedObject = -> Screw_w_Washer_B002
  Placement = pos=(660.4,38.0999,0) rot=(0,0,1;0rad)
FEATURE [App::Link] Link122  label="Screw_w_Washer_B044"
  LinkPlacement = pos=(508,38.1,0) rot=(0,0,1;0rad)
  LinkedObject = -> Screw_w_Washer_B002
  Placement = pos=(508,38.1,0) rot=(0,0,1;0rad)
FEATURE [App::Link] Link123  label="Screw_w_Washer_B045"
  LinkTransform = true
  LinkedObject = -> Link116
FEATURE [App::Link] Link124  label="Screw_w_Washer_B046"
  LinkTransform = true
  LinkedObject = -> Link117
FEATURE [App::Link] Link125  label="Screw_w_Washer_B047"
  LinkTransform = true
  LinkedObject = -> Link118
FEATURE [App::Link] Link126  label="Screw_w_Washer_B048"
  LinkTransform = true
  LinkedObject = -> Link119
FEATURE [App::Link] Link127  label="Screw_w_Washer_B049"
  LinkTransform = true
  LinkedObject = -> Link120
FEATURE [App::Link] Link128  label="Screw_w_Washer_B050"
  LinkTransform = true
  LinkedObject = -> Link121
FEATURE [App::Link] Link129  label="Screw_w_Washer_B051"
  LinkTransform = true
  LinkedObject = -> Link122
FEATURE [App::LinkGroup] LinkGroup012
  ElementList = -> [Link123,Link124,Link125,Link126,Link127,Link128,Link129]
  LinkMode = 1
  Placement = pos=(0,736.6,-7.7486e-07) rot=(0,0,1;0rad)
FEATURE [App::LinkGroup] LinkGroup013  label="Lid_LinkGroup"
  ElementList = -> [Extrude019,Extrude020,Extrude021,Link103,Link104,Screw_w_Washer_B002,Link105,Link106,Link107,Link108,Link109,LinkGroup011,Link116,Link117,Link118,Link119,Link120,Link121,Link122,LinkGroup012,Sketch019,Sketch020,Sketch021]
  LinkMode = 0
  Placement = pos=(-9.20296e-05,831.782,46.832) rot=(0.57735,0.57735,-0.57735;2.0944rad)
FEATURE [Mesh::Feature] _6582_5500W_Portable_Gas_Generator_v1  label="16582_5500W_Portable_Gas_Generator_v1"
  Placement = pos=(395.287,-1.187e-13,-467.35) rot=(-1,0,0;1.5708rad)
FEATURE [App::Link] Link130  label="Screw_w_Washer_D004"
  LinkPlacement = pos=(812.8,736.601,-19.05) rot=(0,-1,0;1.5708rad)
  LinkedObject = -> Screw_w_Washer_D001
  Placement = pos=(812.8,736.601,-19.05) rot=(0,-1,0;1.5708rad)
FEATURE [App::Link] Link131  label="Screw_w_Washer_D005"
  LinkPlacement = pos=(812.8,406.4,-19.0501) rot=(-0.707107,0,0.707107;3.14159rad)
  LinkedObject = -> Screw_w_Washer_D001
  Placement = pos=(812.8,406.4,-19.0501) rot=(-0.707107,0,0.707107;3.14159rad)
FEATURE [App::Link] Link132  label="Screw_w_Washer_D006"
  LinkPlacement = pos=(812.8,406.4,857.25) rot=(-0.707107,0,0.707107;3.14159rad)
  LinkedObject = -> Link131
  Placement = pos=(812.8,406.4,857.25) rot=(-0.707107,0,0.707107;3.14159rad)
FEATURE [App::Link] Link133  label="Screw_w_Washer_D007"
  LinkPlacement = pos=(812.8,736.601,857.25) rot=(0,-1,0;1.5708rad)
  LinkedObject = -> Link130
  Placement = pos=(812.8,736.601,857.25) rot=(0,-1,0;1.5708rad)
FEATURE [App::Link] Link134  label="Screw_w_Washer_D008"
  LinkPlacement = pos=(812.206,25.3999,857.25) rot=(0,-1,0;1.5708rad)
  LinkedObject = -> Screw_w_Washer_D001
  Placement = pos=(812.206,25.3999,857.25) rot=(0,-1,0;1.5708rad)
FEATURE [Part::Feature] Screw_w_Washer_D001  label="Screw_w_Washer_D003"
  Placement = pos=(812.206,25.4,-19.05) rot=(0,-1,0;1.5708rad)
  shape: bbox 67.97 x 25.4 x 25.4 mm, 30 faces (baked)
FEATURE [App::LinkGroup] LinkGroup015  label="Door_Screws"
  ElementList = -> [Link130,Link131,Link132,Link133,Link134,Screw_w_Washer_D001]
  LinkMode = 0
  Placement = pos=(-0.00012207,8.7738e-05,-876.3) rot=(0,0,1;0rad)
FEATURE [App::LinkGroup] LinkGroup016  label="Door_Screws_2"
  ElementList = -> [LinkGroup015]
  LinkMode = 0
  Placement = pos=(813.927,-7.9155e-05,-914.4) rot=(0,1,0;3.14159rad)
FEATURE [App::LinkGroup] LinkGroup014  label="Side_Walls_LinkGroup"
  ElementList = -> [Extrude001,Link102,LinkGroup015,LinkGroup016]
  LinkMode = 0
